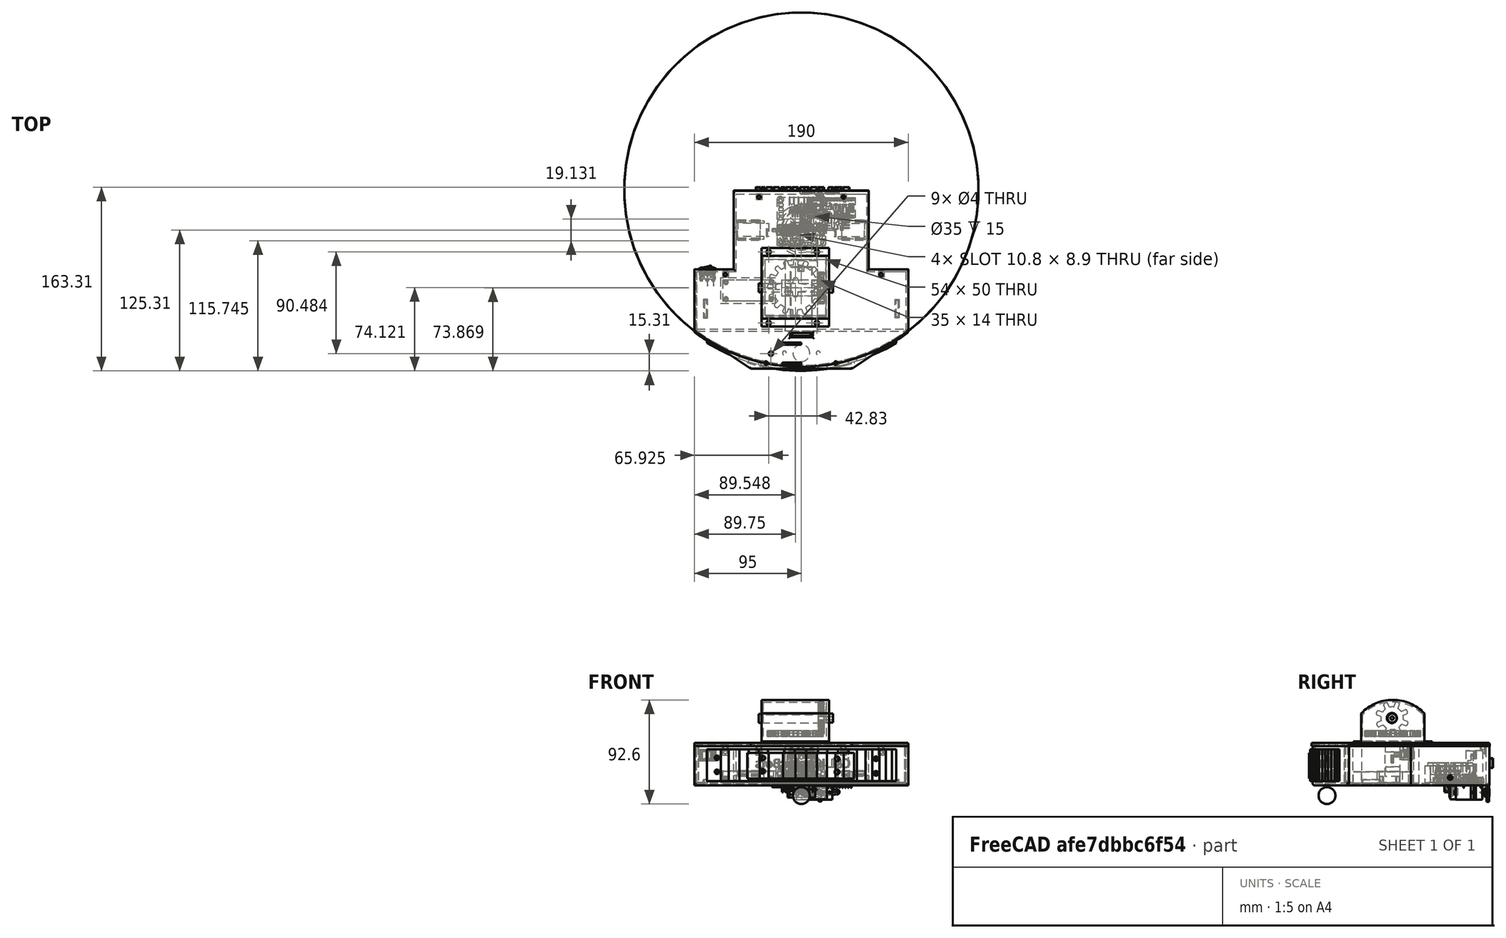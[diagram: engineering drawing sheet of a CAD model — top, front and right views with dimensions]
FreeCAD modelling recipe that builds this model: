
FCSTD DOCUMENT  (FreeCAD 0.20R29410 (Git))
Label: zero_bot
License: All rights reserved
LicenseURL: http://en.wikipedia.org/wiki/All_rights_reserved
objects: Part::Feature×121, Part::Extrusion×56, Sketcher::SketchObject×48, Part::Cut×30, Part::MultiFuse×23, App::Part×10, Part::Box×3, Part::Chamfer×2, Mesh::Feature×2, Part::Part2DObjectPython×1, Part::Fuse×1, Part::Fillet×1, Part::Thickness×1, Part::Sphere×1
note: 288 computed .brp shape members not serialized (recipe doc carries the construction recipe); baked Part::Feature solids carry a one-line shape summary decoded from their .brp

FEATURE [Part::Feature] Part__Feature101  label="Lid Screw Hole001"
  Placement = pos=(159.5,0,0) rot=(0,0,1;0rad)
  shape: bbox 5 x 5 x 8.25 mm, 13 faces (baked)
FEATURE [Part::Feature] Part__Feature102  label="Lid Screw Hole002"
  Placement = pos=(51,69,0) rot=(0,0,1;0rad)
  shape: bbox 5 x 5 x 8.25 mm, 13 faces (baked)
FEATURE [Part::Feature] Part__Feature103  label="Lid Screw Hole003"
  Placement = pos=(126,69,0) rot=(0,0,1;0rad)
  shape: bbox 5 x 5 x 8.25 mm, 13 faces (baked)
FEATURE [Part::Feature] Part__Feature104  label="Lid Screw Hole004"
  Placement = pos=(-120,-158,0) rot=(0,0,1;3.14159rad)
  shape: bbox 5 x 5 x 8.25 mm, 13 faces (baked)
FEATURE [Part::Feature] Part__Feature105  label="Lid Screw Hole005"
  Placement = pos=(-58,-158,0) rot=(0,0,1;3.14159rad)
  shape: bbox 5 x 5 x 8.25 mm, 13 faces (baked)
FEATURE [Part::Feature] Part__Feature106  label="Lid Screw Hole006"
  Placement = pos=(88,5,0) rot=(0,0,1;0rad)
  shape: bbox 5 x 5 x 8.25 mm, 13 faces (baked)
FEATURE [Part::Part2DObjectPython] ShapeString  # Draft 2D object (typed FeaturePython)
  FontFile = <path>
  MakeFace = true
  Placement = pos=(43.52,35,15.82) rot=(0,0.707107,0.707107;3.14159rad)
  Size = 5
  String = C&L KombatBots
  Tracking = 0
FEATURE [Part::Extrusion] Extrude026  label="RobotText"
  Base = -> ShapeString
  Dir = (1e-16,1,4e-16)
  DirMode = 2
  FaceMakerClass = Part::FaceMakerBullseye
  LengthFwd = 3
  LengthRev = 0
  Solid = false
  Symmetric = false
FEATURE [Sketcher::SketchObject] Sketch001
  FullyConstrained = true
  sketch-geometry (10):
    g0: LineSegment StartX=-60 StartY=35 StartZ=0 EndX=60 EndY=35 EndZ=0
    g1: LineSegment StartX=60 StartY=35 StartZ=0 EndX=60 EndY=-35 EndZ=0
    g2: LineSegment StartX=60 StartY=-35 StartZ=0 EndX=95 EndY=-35 EndZ=0
    g3: LineSegment StartX=95 StartY=-35 StartZ=0 EndX=95 EndY=-90 EndZ=0
    g4: LineSegment StartX=95 StartY=-90 StartZ=0 EndX=45 EndY=-123.166 EndZ=0
    g5: LineSegment StartX=45 StartY=-123.166 StartZ=0 EndX=-45 EndY=-123.166 EndZ=0
    g6: LineSegment StartX=-45 StartY=-123.166 StartZ=0 EndX=-95 EndY=-90 EndZ=0
    g7: LineSegment StartX=-95 StartY=-90 StartZ=0 EndX=-95 EndY=-35 EndZ=0
    g8: LineSegment StartX=-95 StartY=-35 StartZ=0 EndX=-60 EndY=-35 EndZ=0
    g9: LineSegment StartX=-60 StartY=-35 StartZ=0 EndX=-60 EndY=35 EndZ=0
  constraints (29):
    c: Horizontal(g0)
    c: Coincident(g0,g1)
    c: Vertical(g1)
    c: Coincident(g1,g2)
    c: Coincident(g2,g3)
    c: Coincident(g3,g4)
    c: Coincident(g4,g5)
    c: Coincident(g5,g6)
    c: Coincident(g6,g7)
    c: Coincident(g7,g8)
    c: Horizontal(g8)
    c: Coincident(g8,g9)
    c: Coincident(g9,g0)
    c: DistanceX(g0,g0) = 120
    c: Vertical(g9)
    c: DistanceY(g9,g9) = 70
    c: DistanceX(g8,g8) = 35
    c: Vertical(g7)
    c: DistanceX(g5,g5) = 90
    c: Horizontal(g5)
    c: Vertical(g3)
    c: DistanceY(g3,g3) = 55
    c: Horizontal(g2)
    c: Equal(g2,g8)
    c: Equal(g9,g1)
    c: Distance(g4) = 60
    c: Equal(g4,g6)
    c: Equal(g3,g7)
    c: Symmetric(g1,g0,g-1)
FEATURE [Part::Extrusion] Extrude001  label="Floor"
  Base = -> Sketch001
  Dir = (0,0,1)
  DirMode = 2
  FaceMakerClass = Part::FaceMakerBullseye
  LengthFwd = 2
  LengthRev = 0
  Solid = true
  Symmetric = false
FEATURE [Sketcher::SketchObject] Sketch002
  FullyConstrained = true
  sketch-geometry (22):
    g0: LineSegment StartX=-60 StartY=35 StartZ=0 EndX=60 EndY=35 EndZ=0
    g1: LineSegment StartX=60 StartY=35 StartZ=0 EndX=60 EndY=-35 EndZ=0
    g2: LineSegment StartX=60 StartY=-35 StartZ=0 EndX=95 EndY=-35 EndZ=0
    g3: LineSegment StartX=95 StartY=-35 StartZ=0 EndX=95 EndY=-90 EndZ=0
    g4: LineSegment StartX=95 StartY=-90 StartZ=0 EndX=45 EndY=-123.166 EndZ=0
    g5: LineSegment StartX=45 StartY=-123.166 StartZ=0 EndX=-45 EndY=-123.166 EndZ=0
    g6: LineSegment StartX=-45 StartY=-123.166 StartZ=0 EndX=-95 EndY=-90 EndZ=0
    g7: LineSegment StartX=-95 StartY=-90 StartZ=0 EndX=-95 EndY=-35 EndZ=0
    g8: LineSegment StartX=-95 StartY=-35 StartZ=0 EndX=-60 EndY=-35 EndZ=0
    g9: LineSegment StartX=-60 StartY=-35 StartZ=0 EndX=-60 EndY=35 EndZ=0
    g10: LineSegment StartX=-58 StartY=32 StartZ=0 EndX=58 EndY=32 EndZ=0
    g11: LineSegment StartX=58 StartY=32 StartZ=0 EndX=58 EndY=-37 EndZ=0
    g12: LineSegment StartX=58 StartY=-37 StartZ=0 EndX=93 EndY=-37 EndZ=0
    g13: LineSegment StartX=93 StartY=-37 StartZ=0 EndX=93 EndY=-89.3266 EndZ=0
    g14: LineSegment StartX=93 StartY=-89.3266 StartZ=0 EndX=45 EndY=-121.166 EndZ=0
    g15: LineSegment StartX=45 StartY=-121.166 StartZ=0 EndX=-45 EndY=-121.166 EndZ=0
    g16: LineSegment StartX=-45 StartY=-121.166 StartZ=0 EndX=-93 EndY=-89.3266 EndZ=0
    g17: LineSegment StartX=-93 StartY=-89.3266 StartZ=0 EndX=-93 EndY=-37 EndZ=0
    g18: LineSegment StartX=-93 StartY=-37 StartZ=0 EndX=-58 EndY=-37 EndZ=0
    g19: LineSegment StartX=-58 StartY=-37 StartZ=0 EndX=-58 EndY=32 EndZ=0
    g20: LineSegment StartX=-45 StartY=-121.166 StartZ=0 EndX=-45 EndY=-123.166 EndZ=0
    g21: LineSegment StartX=45 StartY=-121.166 StartZ=0 EndX=45 EndY=-123.166 EndZ=0
  constraints (63):
    c: Horizontal(g0)
    c: Coincident(g0,g1)
    c: Vertical(g1)
    c: Coincident(g1,g2)
    c: Horizontal(g2)
    c: Coincident(g2,g3)
    c: Vertical(g3)
    c: Coincident(g3,g4)
    c: Coincident(g4,g5)
    c: Horizontal(g5)
    c: Coincident(g5,g6)
    c: Coincident(g6,g7)
    c: Vertical(g7)
    c: Coincident(g7,g8)
    c: Horizontal(g8)
    c: Coincident(g8,g9)
    c: Coincident(g9,g0)
    c: Vertical(g9)
    c: Symmetric(g0,g1,g-1)
    c: DistanceX(g0,g0) = 120
    c: DistanceY(g1,g1) = 70
    c: Equal(g9,g1)
    c: DistanceX(g2,g2) = 35
    c: Equal(g2,g8)
    c: DistanceY(g3,g3) = 55
    c: DistanceX(g5,g5) = 90
    c: Distance(g4) = 60
    c: Equal(g4,g6)
    c: Equal(g3,g7)
    c: Horizontal(g10)
    c: Coincident(g11,g10)
    c: Vertical(g11)
    c: Coincident(g11,g12)
    c: Horizontal(g12)
    c: Coincident(g12,g13)
    c: Vertical(g13)
    c: Coincident(g13,g14)
    c: Coincident(g14,g15)
    c: Horizontal(g15)
    c: Coincident(g15,g16)
    c: Coincident(g16,g17)
    c: Vertical(g17)
    c: Coincident(g17,g18)
    c: Horizontal(g18)
    c: Coincident(g18,g19)
    c: Coincident(g19,g10)
    c: Vertical(g19)
    c: Distance(g10,g0) = 3
    c: Distance(g10,g9) = 2
    c: Distance(g17,g8) = 2
    c: Distance(g16,g7) = 2
    c: Distance(g15,g5) = 2
    c: Distance(g13,g3) = 2
    c: Distance(g12,g2) = 2
    c: Distance(g10,g1) = 2
    c: Coincident(g20,g15)
    c: Coincident(g20,g5)
    c: Coincident(g21,g14)
    c: Coincident(g21,g4)
    c: Vertical(g21)
    c: Vertical(g20)
    c: Parallel(g16,g6)
    c: Parallel(g14,g4)
FEATURE [Part::Extrusion] Extrude002  label="Walls"
  Base = -> Sketch002
  Dir = (0,0,1)
  DirMode = 2
  FaceMakerClass = Part::FaceMakerBullseye
  LengthFwd = 35
  LengthRev = 0
  Solid = true
  Symmetric = false
FEATURE [Part::MultiFuse] Fusion004  label="Body"
  Refine = true
  Shapes = -> [Extrude002,Extrude001]
FEATURE [Sketcher::SketchObject] Sketch003
  FullyConstrained = false
  MapMode = 5
  Placement = pos=(0,0,2) rot=(0,0,1;0rad)
  Support = -> [Fusion004]
  sketch-geometry (36):
    g0: GeomPoint X=25 Y=0 Z=0
    g1: LineSegment StartX=33 StartY=6 StartZ=0 EndX=58 EndY=6 EndZ=0
    g2: LineSegment StartX=58 StartY=6 StartZ=0 EndX=58 EndY=8 EndZ=0
    g3: LineSegment StartX=58 StartY=8 StartZ=0 EndX=33 EndY=8 EndZ=0
    g4: LineSegment StartX=33 StartY=8 StartZ=0 EndX=33 EndY=6 EndZ=0
    g5: GeomPoint X=-25 Y=0 Z=0
    g6: LineSegment StartX=33 StartY=6 StartZ=0 EndX=25 EndY=0 EndZ=0
    g7: GeomPoint X=25 Y=0 Z=0
    g8: LineSegment StartX=32.5993 StartY=-6.5 StartZ=0 EndX=25 EndY=0 EndZ=0
    g9: GeomPoint X=-25 Y=0 Z=0
    g10: GeomPoint X=-25 Y=0 Z=0
    g11: GeomPoint X=25 Y=0 Z=0
    g12: LineSegment StartX=33 StartY=-6 StartZ=0 EndX=58 EndY=-6 EndZ=0
    g13: LineSegment StartX=58 StartY=-6 StartZ=0 EndX=58 EndY=-8 EndZ=0
    g14: LineSegment StartX=58 StartY=-8 StartZ=0 EndX=33 EndY=-8 EndZ=0
    g15: LineSegment StartX=33 StartY=-8 StartZ=0 EndX=33 EndY=-6 EndZ=0
    g16: LineSegment StartX=33 StartY=-6 StartZ=0 EndX=25 EndY=0 EndZ=0
    g17: GeomPoint X=25 Y=0 Z=0
    g18: LineSegment StartX=32.5993 StartY=6.5 StartZ=0 EndX=25 EndY=0 EndZ=0
    g19: GeomPoint X=-25 Y=0 Z=0
    g20: LineSegment StartX=-33 StartY=6 StartZ=0 EndX=-58 EndY=6 EndZ=0
    g21: LineSegment StartX=-58 StartY=6 StartZ=0 EndX=-58 EndY=8 EndZ=0
    g22: LineSegment StartX=-58 StartY=8 StartZ=0 EndX=-33 EndY=8 EndZ=0
    g23: LineSegment StartX=-33 StartY=8 StartZ=0 EndX=-33 EndY=6 EndZ=0
    g24: LineSegment StartX=-33 StartY=6 StartZ=0 EndX=-25 EndY=0 EndZ=0
    g25: GeomPoint X=-25 Y=0 Z=0
    g26: LineSegment StartX=-32.5993 StartY=-6.5 StartZ=0 EndX=-25 EndY=0 EndZ=0
    g27: GeomPoint X=-25 Y=0 Z=0
    g28: LineSegment StartX=-33 StartY=-6 StartZ=0 EndX=-58 EndY=-6 EndZ=0
    g29: LineSegment StartX=-58 StartY=-6 StartZ=0 EndX=-58 EndY=-8 EndZ=0
    g30: LineSegment StartX=-58 StartY=-8 StartZ=0 EndX=-33 EndY=-8 EndZ=0
    g31: LineSegment StartX=-33 StartY=-8 StartZ=0 EndX=-33 EndY=-6 EndZ=0
    g32: LineSegment StartX=-33 StartY=-6 StartZ=0 EndX=-25 EndY=0 EndZ=0
    g33: GeomPoint X=-25 Y=0 Z=0
    g34: LineSegment StartX=-32.5993 StartY=6.5 StartZ=0 EndX=-25 EndY=0 EndZ=0
    g35: LineSegment StartX=-33 StartY=8 StartZ=0 EndX=-33 EndY=-8 EndZ=0
  constraints (60):
    c: PointOnObject(g0,g-1)
    c: Distance(g-1,g0) = 25
    c: Coincident(g1,g2)
    c: Coincident(g2,g3)
    c: Coincident(g3,g4)
    c: Coincident(g4,g1)
    c: Horizontal(g1)
    c: Horizontal(g3)
    c: Vertical(g2)
    c: Vertical(g4)
    c: DistanceY(g4,g4) = 2
    c: DistanceX(g1,g1) = 25
    c: Coincident(g6,g1)
    c: Coincident(g6,g0)
    c: Distance(g6) = 10
    c: DistanceY(g-1,g1) = 6
    c: Coincident(g8,g7)
    c: Distance(g8) = 10
    c: Coincident(g12,g13)
    c: Coincident(g13,g14)
    c: Coincident(g14,g15)
    c: Coincident(g15,g12)
    c: Horizontal(g12)
    c: Horizontal(g14)
    c: Vertical(g13)
    c: Vertical(g15)
    c: Coincident(g16,g12)
    c: Coincident(g16,g11)
    c: Distance(g16) = 10
    c: Coincident(g18,g17)
    c: Distance(g18) = 10
    c: Coincident(g20,g21)
    c: Coincident(g21,g22)
    c: Coincident(g22,g23)
    c: Coincident(g23,g20)
    c: Horizontal(g20)
    c: Horizontal(g22)
    c: Vertical(g21)
    c: Vertical(g23)
    c: Coincident(g24,g20)
    c: Coincident(g24,g19)
    c: Distance(g24) = 10
    c: Coincident(g26,g25)
    c: Distance(g26) = 10
    c: Coincident(g28,g29)
    c: Coincident(g29,g30)
    c: Coincident(g30,g31)
    c: Coincident(g31,g28)
    c: Horizontal(g28)
    c: Horizontal(g30)
    c: Vertical(g29)
    c: Vertical(g31)
    c: Coincident(g32,g28)
    c: Coincident(g32,g27)
    c: Distance(g32) = 10
    c: Coincident(g34,g33)
    c: Distance(g34) = 10
    c: Coincident(g35,g22)
    c: Coincident(g35,g30)
    c: Vertical(g35)
FEATURE [Part::Extrusion] Extrude003  label="motorWalls"
  Base = -> Sketch003
  Dir = (0,0,1)
  DirMode = 2
  FaceMakerClass = Part::FaceMakerBullseye
  LengthFwd = 10
  LengthRev = 0
  Solid = true
  Symmetric = false
FEATURE [Sketcher::SketchObject] Sketch004
  FullyConstrained = false
  MapMode = 5
  Placement = pos=(0,0,2) rot=(0,0,1;0rad)
  Support = -> [Fusion004]
  sketch-geometry (10):
    g0: LineSegment StartX=-31 StartY=6 StartZ=0 EndX=-29 EndY=6 EndZ=0
    g1: LineSegment StartX=-29 StartY=6 StartZ=0 EndX=-29 EndY=-6 EndZ=0
    g2: LineSegment StartX=-29 StartY=-6 StartZ=0 EndX=-31 EndY=-6 EndZ=0
    g3: LineSegment StartX=-31 StartY=-6 StartZ=0 EndX=-31 EndY=6 EndZ=0
    g4: GeomPoint X=-30 Y=0 Z=0
    g5: LineSegment StartX=31 StartY=6 StartZ=0 EndX=29 EndY=6 EndZ=0
    g6: LineSegment StartX=29 StartY=6 StartZ=0 EndX=29 EndY=-6 EndZ=0
    g7: LineSegment StartX=29 StartY=-6 StartZ=0 EndX=31 EndY=-6 EndZ=0
    g8: LineSegment StartX=31 StartY=-6 StartZ=0 EndX=31 EndY=6 EndZ=0
    g9: GeomPoint X=30 Y=0 Z=0
  constraints (22):
    c: Coincident(g0,g1)
    c: Coincident(g1,g2)
    c: Coincident(g2,g3)
    c: Coincident(g3,g0)
    c: Horizontal(g0)
    c: Horizontal(g2)
    c: Vertical(g1)
    c: Vertical(g3)
    c: PointOnObject(g4,g-1)
    c: Distance(g-1,g4) = 30
    c: Symmetric(g0,g2,g4)
    c: DistanceX(g0,g0) = 2
    c: DistanceY(g1,g1) = 12
    c: Coincident(g5,g6)
    c: Coincident(g6,g7)
    c: Coincident(g7,g8)
    c: Coincident(g8,g5)
    c: Horizontal(g5)
    c: Horizontal(g7)
    c: Vertical(g6)
    c: Vertical(g8)
    c: Symmetric(g5,g7,g9)
FEATURE [Part::Extrusion] Extrude004
  Base = -> Sketch004
  Dir = (0,0,1)
  DirMode = 2
  FaceMakerClass = Part::FaceMakerBullseye
  LengthFwd = 3
  LengthRev = 0
  Solid = true
  Symmetric = false
FEATURE [Part::Chamfer] Chamfer  label="MotorSlotter"
  Base = -> Extrude004
  Edges = 2 edges r=1: [Edge12,Edge24]
FEATURE [Part::MultiFuse] Fusion001  label="MotorHolders"
  Refine = true
  Shapes = -> [Chamfer,Extrude003]
FEATURE [Part::MultiFuse] Fusion005
  Refine = true
  Shapes = -> [Fusion001,Fusion004]
FEATURE [Sketcher::SketchObject] Sketch005
  FullyConstrained = true
  MapMode = 5
  Placement = pos=(0,0,2) rot=(0,0,1;0rad)
  Support = -> [Fusion005]
  sketch-geometry (8):
    g0: Circle CenterX=-18.8 CenterY=26.75 CenterZ=0 NormalX=0 NormalY=0 NormalZ=1 AngleXU=0 Radius=3
    g1: Circle CenterX=-18.8 CenterY=26.75 CenterZ=0 NormalX=0 NormalY=0 NormalZ=1 AngleXU=0 Radius=1.5
    g2: Circle CenterX=18.8 CenterY=26.75 CenterZ=0 NormalX=0 NormalY=0 NormalZ=1 AngleXU=0 Radius=3
    g3: Circle CenterX=18.8 CenterY=26.75 CenterZ=0 NormalX=0 NormalY=0 NormalZ=1 AngleXU=0 Radius=1.5
    g4: Circle CenterX=18.8 CenterY=-11 CenterZ=0 NormalX=0 NormalY=0 NormalZ=1 AngleXU=0 Radius=3
    g5: Circle CenterX=18.8 CenterY=-11 CenterZ=0 NormalX=0 NormalY=0 NormalZ=1 AngleXU=0 Radius=1.5
    g6: Circle CenterX=-18.8 CenterY=-11 CenterZ=0 NormalX=0 NormalY=0 NormalZ=1 AngleXU=0 Radius=3
    g7: Circle CenterX=-18.8 CenterY=-11 CenterZ=0 NormalX=0 NormalY=0 NormalZ=1 AngleXU=0 Radius=1.5
  constraints (20):
    c: Coincident(g1,g0)
    c: Coincident(g3,g2)
    c: Coincident(g5,g4)
    c: Coincident(g7,g6)
    c: DistanceX(g-2,g6) = -18.8
    c: Diameter(g7) = 3
    c: Diameter(g6) = 6
    c: DistanceY(g-1,g6) = -11
    c: DistanceY(g-1,g4) = -11
    c: DistanceX(g-2,g4) = 18.8
    c: Diameter(g5) = 3
    c: Diameter(g4) = 6
    c: DistanceY(g-1,g2) = 26.75
    c: DistanceY(g-1,g0) = 26.75
    c: DistanceX(g-2,g2) = 18.8
    c: DistanceX(g-2,g0) = -18.8
    c: Diameter(g1) = 3
    c: Diameter(g0) = 6
    c: Diameter(g2) = 6
    c: Diameter(g3) = 3
FEATURE [Part::Extrusion] Extrude005  label="L289N Holder"
  Base = -> Sketch005
  Dir = (0,0,1)
  DirMode = 2
  FaceMakerClass = Part::FaceMakerBullseye
  LengthFwd = 4
  LengthRev = 0
  Solid = true
  Symmetric = false
FEATURE [Part::MultiFuse] Fusion006
  Refine = true
  Shapes = -> [Extrude005,Fusion005]
FEATURE [Sketcher::SketchObject] Sketch006
  FullyConstrained = true
  MapMode = 5
  Placement = pos=(60,0,0) rot=(0.57735,0.57735,0.57735;2.0944rad)
  Support = -> [Fusion006]
  sketch-geometry (1):
    g0: Circle CenterX=0 CenterY=7 CenterZ=0 NormalX=0 NormalY=0 NormalZ=1 AngleXU=0 Radius=2
  constraints (3):
    c: PointOnObject(g0,g-2)
    c: Diameter(g0) = 4
    c: Distance(g0,g-1) = 7
FEATURE [Part::Extrusion] Extrude006
  Base = -> Sketch006
  Dir = (1,0,0)
  DirMode = 2
  FaceMakerClass = Part::FaceMakerBullseye
  LengthFwd = 10
  LengthRev = 0
  Solid = true
  Symmetric = true
FEATURE [Sketcher::SketchObject] Sketch007
  FullyConstrained = true
  MapMode = 5
  Placement = pos=(-60,0,0) rot=(0.57735,-0.57735,-0.57735;2.0944rad)
  Support = -> [Fusion006]
  sketch-geometry (1):
    g0: Circle CenterX=0 CenterY=7 CenterZ=0 NormalX=0 NormalY=0 NormalZ=1 AngleXU=0 Radius=2
  constraints (3):
    c: PointOnObject(g0,g-2)
    c: Diameter(g0) = 4
    c: Distance(g-1,g0) = 7
FEATURE [Part::Extrusion] Extrude007
  Base = -> Sketch007
  Dir = (-1,0,0)
  DirMode = 2
  FaceMakerClass = Part::FaceMakerBullseye
  LengthFwd = 10
  LengthRev = 0
  Solid = true
  Symmetric = true
FEATURE [Part::MultiFuse] Fusion007  label="Motor Gaps"
  Refine = true
  Shapes = -> [Extrude006,Extrude007]
FEATURE [Part::Cut] Cut005
  Base = -> Fusion006
  Refine = true
  Tool = -> Fusion007
FEATURE [Sketcher::SketchObject] Sketch008
  FullyConstrained = false
  MapMode = 5
  Placement = pos=(0,-35,0) rot=(0,0.707107,0.707107;3.14159rad)
  Support = -> [Cut005]
  sketch-geometry (4):
    g0: LineSegment StartX=90.8327 StartY=31.6367 StartZ=0 EndX=76.0827 EndY=31.6367 EndZ=0
    g1: LineSegment StartX=76.0827 StartY=31.6367 StartZ=0 EndX=76.0827 EndY=21.8867 EndZ=0
    g2: LineSegment StartX=76.0827 StartY=21.8867 StartZ=0 EndX=90.8327 EndY=21.8867 EndZ=0
    g3: LineSegment StartX=90.8327 StartY=21.8867 StartZ=0 EndX=90.8327 EndY=31.6367 EndZ=0
  constraints (8):
    c: Coincident(g0,g1)
    c: Coincident(g1,g2)
    c: Coincident(g2,g3)
    c: Coincident(g3,g0)
    c: Horizontal(g0)
    c: Horizontal(g2)
    c: Vertical(g1)
    c: Vertical(g3)
FEATURE [Part::Extrusion] Extrude008  label="InterruptGap"
  Base = -> Sketch008
  Dir = (0,1,-2e-16)
  DirMode = 2
  FaceMakerClass = Part::FaceMakerBullseye
  LengthFwd = 10
  LengthRev = 0
  Solid = true
  Symmetric = true
FEATURE [Part::Cut] Cut006
  Base = -> Cut005
  Refine = true
  Tool = -> Extrude008
FEATURE [Sketcher::SketchObject] Sketch009
  FullyConstrained = false
  MapMode = 5
  Placement = pos=(0,0,2) rot=(0,0,1;0rad)
  Support = -> [Cut006]
  sketch-geometry (20):
    g0: LineSegment StartX=83.4 StartY=-61.75 StartZ=0 EndX=87 EndY=-61.75 EndZ=0
    g1: LineSegment StartX=87 StartY=-61.75 StartZ=0 EndX=87 EndY=-78.25 EndZ=0
    g2: LineSegment StartX=87 StartY=-78.25 StartZ=0 EndX=83.4 EndY=-78.25 EndZ=0
    g3: LineSegment StartX=83.4 StartY=-78.25 StartZ=0 EndX=83.4 EndY=-61.75 EndZ=0
    g4: LineSegment StartX=84.4 StartY=-62.6 StartZ=0 EndX=86 EndY=-62.6 EndZ=0
    g5: LineSegment StartX=86 StartY=-62.6 StartZ=0 EndX=86 EndY=-77.4 EndZ=0
    g6: LineSegment StartX=86 StartY=-77.4 StartZ=0 EndX=84.4 EndY=-77.4 EndZ=0
    g7: LineSegment StartX=84.4 StartY=-77.4 StartZ=0 EndX=84.4 EndY=-62.6 EndZ=0
    g8: GeomPoint X=93 Y=-70 Z=0
    g9: LineSegment StartX=-0.686599 StartY=-70 StartZ=0 EndX=93 EndY=-70 EndZ=0
    g10: LineSegment StartX=-83.4 StartY=-61.75 StartZ=0 EndX=-87 EndY=-61.75 EndZ=0
    g11: LineSegment StartX=-87 StartY=-61.75 StartZ=0 EndX=-87 EndY=-78.25 EndZ=0
    g12: LineSegment StartX=-87 StartY=-78.25 StartZ=0 EndX=-83.4 EndY=-78.25 EndZ=0
    g13: LineSegment StartX=-83.4 StartY=-78.25 StartZ=0 EndX=-83.4 EndY=-61.75 EndZ=0
    g14: LineSegment StartX=-84.4 StartY=-62.6 StartZ=0 EndX=-86 EndY=-62.6 EndZ=0
    g15: LineSegment StartX=-86 StartY=-62.6 StartZ=0 EndX=-86 EndY=-77.4 EndZ=0
    g16: LineSegment StartX=-86 StartY=-77.4 StartZ=0 EndX=-84.4 EndY=-77.4 EndZ=0
    g17: LineSegment StartX=-84.4 StartY=-77.4 StartZ=0 EndX=-84.4 EndY=-62.6 EndZ=0
    g18: GeomPoint X=-93 Y=-70 Z=0
    g19: LineSegment StartX=0.686599 StartY=-70 StartZ=0 EndX=-93 EndY=-70 EndZ=0
  constraints (46):
    c: Coincident(g0,g1)
    c: Coincident(g1,g2)
    c: Coincident(g2,g3)
    c: Coincident(g3,g0)
    c: Horizontal(g0)
    c: Horizontal(g2)
    c: Vertical(g1)
    c: Vertical(g3)
    c: Coincident(g4,g5)
    c: Coincident(g5,g6)
    c: Coincident(g6,g7)
    c: Coincident(g7,g4)
    c: Horizontal(g4)
    c: Horizontal(g6)
    c: Vertical(g7)
    c: DistanceX(g-2,g8) = 93
    c: DistanceY(g-1,g8) = -70
    c: Distance(g8,g1) = 6
    c: Coincident(g9,g8)
    c: Symmetric(g1,g0,g9)
    c: DistanceY(g1,g1) = 16.5
    c: Symmetric(g4,g5,g9)
    c: DistanceY(g5,g5) = 14.8
    c: DistanceX(g0,g0) = 3.6
    c: DistanceX(g4,g4) = 1.6
    c: Distance(g4,g1) = 1
    c: Coincident(g10,g11)
    c: Coincident(g11,g12)
    c: Coincident(g12,g13)
    c: Coincident(g13,g10)
    c: Horizontal(g10)
    c: Horizontal(g12)
    c: Vertical(g11)
    c: Vertical(g13)
    c: Coincident(g14,g15)
    c: Coincident(g15,g16)
    c: Coincident(g16,g17)
    c: Coincident(g17,g14)
    c: Horizontal(g14)
    c: Horizontal(g16)
    c: Vertical(g17)
    c: Distance(g18,g11) = 6
    c: Coincident(g19,g18)
    c: Symmetric(g11,g10,g19)
    c: Symmetric(g14,g15,g19)
    c: Distance(g14,g11) = 1
FEATURE [Part::Extrusion] Extrude009  label="HitSensorHolders"
  Base = -> Sketch009
  Dir = (0,0,1)
  DirMode = 2
  FaceMakerClass = Part::FaceMakerBullseye
  LengthFwd = 3
  LengthRev = 0
  Solid = true
  Symmetric = false
FEATURE [Part::MultiFuse] Fusion008
  Refine = true
  Shapes = -> [Cut006,Extrude009]
FEATURE [Sketcher::SketchObject] Sketch010
  FullyConstrained = true
  sketch-geometry (11):
    g0: LineSegment StartX=-14.5 StartY=-78.5 StartZ=0 EndX=-9.5 EndY=-78.5 EndZ=0
    g1: LineSegment StartX=-9.5 StartY=-78.5 StartZ=0 EndX=-9.5 EndY=-32.5 EndZ=0
    g2: LineSegment StartX=-9.5 StartY=-32.5 StartZ=0 EndX=9.5 EndY=-32.5 EndZ=0
    g3: LineSegment StartX=9.5 StartY=-32.5 StartZ=0 EndX=9.5 EndY=-86.5 EndZ=0
    g4: LineSegment StartX=9.5 StartY=-86.5 StartZ=0 EndX=-14.5 EndY=-86.5 EndZ=0
    g5: LineSegment StartX=-14.5 StartY=-86.5 StartZ=0 EndX=-14.5 EndY=-91.5 EndZ=0
    g6: LineSegment StartX=-14.5 StartY=-91.5 StartZ=0 EndX=14.5 EndY=-91.5 EndZ=0
    g7: LineSegment StartX=14.5 StartY=-91.5 StartZ=0 EndX=14.5 EndY=-27.5 EndZ=0
    g8: LineSegment StartX=14.5 StartY=-27.5 StartZ=0 EndX=-14.5 EndY=-27.5 EndZ=0
    g9: LineSegment StartX=-14.5 StartY=-27.5 StartZ=0 EndX=-14.5 EndY=-78.5 EndZ=0
    g10: GeomPoint X=0 Y=-59.5 Z=0
  constraints (30):
    c: Horizontal(g0)
    c: Coincident(g0,g1)
    c: Vertical(g1)
    c: Coincident(g1,g2)
    c: Horizontal(g2)
    c: Coincident(g2,g3)
    c: Vertical(g3)
    c: Coincident(g3,g4)
    c: Horizontal(g4)
    c: Coincident(g4,g5)
    c: Vertical(g5)
    c: Coincident(g5,g6)
    c: Horizontal(g6)
    c: Coincident(g6,g7)
    c: Vertical(g7)
    c: Coincident(g7,g8)
    c: Horizontal(g8)
    c: Coincident(g8,g9)
    c: Coincident(g9,g0)
    c: Vertical(g9)
    c: DistanceX(g2,g2) = 19
    c: PointOnObject(g10,g-2)
    c: DistanceY(g10,g-1) = 59.5
    c: Symmetric(g3,g1,g10)
    c: Symmetric(g6,g8,g10)
    c: DistanceX(g8,g8) = 29
    c: DistanceY(g3,g3) = 54
    c: DistanceY(g7,g7) = 64
    c: DistanceY(g1,g1) = 46
    c: DistanceX(g6,g6) = 29
FEATURE [Part::Extrusion] Extrude010  label="Battery Gap"
  Base = -> Sketch010
  Dir = (0,0,1)
  DirMode = 2
  FaceMakerClass = Part::FaceMakerBullseye
  LengthFwd = 35
  LengthRev = 0
  Solid = true
  Symmetric = false
FEATURE [Part::MultiFuse] Fusion009
  Refine = true
  Shapes = -> [Extrude010,Fusion008]
FEATURE [Sketcher::SketchObject] Sketch011
  FullyConstrained = false
  MapMode = 5
  Placement = pos=(0,0,2) rot=(0,0,1;0rad)
  Support = -> [Fusion009]
  sketch-geometry (13):
    g0: LineSegment StartX=-52.8 StartY=-54 StartZ=0 EndX=0 EndY=-54 EndZ=0
    g1: LineSegment StartX=-52.8 StartY=-54 StartZ=0 EndX=-84.748 EndY=-54 EndZ=0
    g2: Circle CenterX=-66.9946 CenterY=-46.5 CenterZ=0 NormalX=0 NormalY=0 NormalZ=1 AngleXU=0 Radius=1
    g3: Circle CenterX=-66.9946 CenterY=-46.5 CenterZ=0 NormalX=0 NormalY=0 NormalZ=1 AngleXU=0 Radius=2
    g4: Circle CenterX=-66.9946 CenterY=-61.5 CenterZ=0 NormalX=0 NormalY=0 NormalZ=1 AngleXU=0 Radius=1
    g5: Circle CenterX=-66.9946 CenterY=-61.5 CenterZ=0 NormalX=0 NormalY=0 NormalZ=1 AngleXU=0 Radius=2
    g6: GeomPoint X=-25.3 Y=-54 Z=0
    g7: Circle CenterX=-26.6711 CenterY=-46.5 CenterZ=0 NormalX=0 NormalY=0 NormalZ=1 AngleXU=0 Radius=1
    g8: Circle CenterX=-26.6711 CenterY=-46.5 CenterZ=0 NormalX=0 NormalY=0 NormalZ=1 AngleXU=0 Radius=2
    g9: Circle CenterX=-26.6711 CenterY=-61.5 CenterZ=0 NormalX=0 NormalY=0 NormalZ=1 AngleXU=0 Radius=1
    g10: Circle CenterX=-26.6711 CenterY=-61.5 CenterZ=0 NormalX=0 NormalY=0 NormalZ=1 AngleXU=0 Radius=2
    g11: LineSegment StartX=-52.8 StartY=-54 StartZ=0 EndX=0 EndY=-54 EndZ=0
    g12: GeomPoint X=-25.3 Y=-54 Z=0
  constraints (24):
    c: DistanceY(g0,g-1) = 54
    c: PointOnObject(g0,g-2)
    c: Horizontal(g0)
    c: Coincident(g1,g0)
    c: Horizontal(g1)
    c: Coincident(g3,g2)
    c: Diameter(g2) = 2
    c: Diameter(g3) = 4
    c: Distance(g2,g1) = 7.5
    c: Coincident(g5,g4)
    c: Diameter(g4) = 2
    c: Diameter(g5) = 4
    c: PointOnObject(g6,g0)
    c: DistanceX(g6,g-1) = 25.3
    c: Coincident(g8,g7)
    c: Diameter(g7) = 2
    c: Diameter(g8) = 4
    c: Distance(g7,g0) = 7.5
    c: Horizontal(g11)
    c: PointOnObject(g12,g11)
    c: Coincident(g10,g9)
    c: Diameter(g9) = 2
    c: Diameter(g10) = 4
    c: Distance(g9,g11) = 7.5
FEATURE [Part::Extrusion] Extrude011  label="Arduino Holder"
  Base = -> Sketch011
  Dir = (0,0,1)
  DirMode = 2
  FaceMakerClass = Part::FaceMakerBullseye
  LengthFwd = 6
  LengthRev = 0
  Solid = true
  Symmetric = false
FEATURE [Part::MultiFuse] Fusion010
  Refine = true
  Shapes = -> [Fusion009,Extrude011]
FEATURE [Sketcher::SketchObject] Sketch012
  FullyConstrained = true
  MapMode = 5
  Placement = pos=(0,-91.5,0) rot=(1,0,0;1.5708rad)
  Support = -> [Extrude010]
  sketch-geometry (10):
    g0: LineSegment StartX=8 StartY=35 StartZ=0 EndX=10 EndY=35 EndZ=0
    g1: LineSegment StartX=10 StartY=35 StartZ=0 EndX=10 EndY=2 EndZ=0
    g2: LineSegment StartX=10 StartY=2 StartZ=0 EndX=-10 EndY=2 EndZ=0
    g3: LineSegment StartX=-10 StartY=2 StartZ=0 EndX=-10 EndY=35 EndZ=0
    g4: LineSegment StartX=-10 StartY=35 StartZ=0 EndX=-8 EndY=35 EndZ=0
    g5: LineSegment StartX=-8 StartY=35 StartZ=0 EndX=-8 EndY=4 EndZ=0
    g6: LineSegment StartX=-8 StartY=4 StartZ=0 EndX=8 EndY=4 EndZ=0
    g7: LineSegment StartX=8 StartY=4 StartZ=0 EndX=8 EndY=35 EndZ=0
    g8: GeomPoint X=0 Y=2 Z=0
    g9: LineSegment StartX=0 StartY=2 StartZ=0 EndX=0 EndY=0 EndZ=0
  constraints (28):
    c: Horizontal(g0)
    c: Coincident(g0,g1)
    c: Vertical(g1)
    c: Coincident(g1,g2)
    c: Coincident(g2,g3)
    c: Vertical(g3)
    c: Coincident(g3,g4)
    c: Horizontal(g4)
    c: Coincident(g4,g5)
    c: Vertical(g5)
    c: Coincident(g5,g6)
    c: Horizontal(g6)
    c: Coincident(g6,g7)
    c: Coincident(g7,g0)
    c: Vertical(g7)
    c: DistanceX(g0,g0) = 2
    c: Equal(g4,g0)
    c: DistanceX(g6,g6) = 16
    c: DistanceY(g1,g1) = 33
    c: Equal(g3,g1)
    c: Distance(g6,g2) = 2
    c: Horizontal(g2)
    c: PointOnObject(g8,g2)
    c: DistanceX(g8,g1) = 10
    c: DistanceY(g-1,g1) = 2
    c: Coincident(g9,g8)
    c: Coincident(g9,g-1)
    c: Vertical(g9)
FEATURE [Part::Extrusion] Extrude012  label="Bluetooth Module Holder"
  Base = -> Sketch012
  Dir = (0,-1,2e-16)
  DirMode = 2
  FaceMakerClass = Part::FaceMakerBullseye
  LengthFwd = 4
  LengthRev = 0
  Solid = true
  Symmetric = false
FEATURE [Part::MultiFuse] Fusion011
  Refine = true
  Shapes = -> [Fusion010,Extrude012]
FEATURE [Sketcher::SketchObject] Sketch013
  FullyConstrained = false
  MapMode = 5
  Placement = pos=(4.907e-13,3.136e-13,35) rot=(0,0,1;0rad)
  Support = -> [Fusion011]
  sketch-geometry (8):
    g0: LineSegment StartX=8 StartY=-92.5 StartZ=0 EndX=8.5 EndY=-92.5 EndZ=0
    g1: LineSegment StartX=8.5 StartY=-92.5 StartZ=0 EndX=8.5 EndY=-94.7 EndZ=0
    g2: LineSegment StartX=8.5 StartY=-94.7 StartZ=0 EndX=8 EndY=-94.7 EndZ=0
    g3: LineSegment StartX=8 StartY=-94.7 StartZ=0 EndX=8 EndY=-92.5 EndZ=0
    g4: LineSegment StartX=-8 StartY=-92.5 StartZ=0 EndX=-8.5 EndY=-92.5 EndZ=0
    g5: LineSegment StartX=-8.5 StartY=-92.5 StartZ=0 EndX=-8.5 EndY=-94.7 EndZ=0
    g6: LineSegment StartX=-8.5 StartY=-94.7 StartZ=0 EndX=-8 EndY=-94.7 EndZ=0
    g7: LineSegment StartX=-8 StartY=-94.7 StartZ=0 EndX=-8 EndY=-92.5 EndZ=0
  constraints (20):
    c: Coincident(g0,g1)
    c: Coincident(g1,g2)
    c: Coincident(g2,g3)
    c: Coincident(g3,g0)
    c: Horizontal(g0)
    c: Horizontal(g2)
    c: Vertical(g1)
    c: Vertical(g3)
    c: DistanceY(g1,g1) = 2.2
    c: DistanceX(g0,g0) = 0.5
    c: DistanceX(g-2,g0) = 8
    c: DistanceY(g-1,g0) = -92.5
    c: Coincident(g4,g5)
    c: Coincident(g5,g6)
    c: Coincident(g6,g7)
    c: Coincident(g7,g4)
    c: Horizontal(g4)
    c: Horizontal(g6)
    c: Vertical(g5)
    c: Vertical(g7)
FEATURE [Part::Extrusion] Extrude013  label="Bluetooth Module Slotter"
  Base = -> Sketch013
  Dir = (1.4e-14,9e-15,1)
  DirMode = 2
  FaceMakerClass = Part::FaceMakerBullseye
  LengthFwd = -32
  LengthRev = 0
  Solid = true
  Symmetric = false
FEATURE [Part::Cut] Cut007
  Base = -> Fusion011
  Refine = true
  Tool = -> Extrude013
FEATURE [Sketcher::SketchObject] Sketch014
  FullyConstrained = false
  MapMode = 5
  Placement = pos=(0,-37,0) rot=(1,0,0;1.5708rad)
  Support = -> [Cut007]
  sketch-geometry (4):
    g0: LineSegment StartX=-91.0267 StartY=31.7549 StartZ=0 EndX=-86.0267 EndY=31.7549 EndZ=0
    g1: LineSegment StartX=-86.0267 StartY=31.7549 StartZ=0 EndX=-86.0267 EndY=26.7549 EndZ=0
    g2: LineSegment StartX=-86.0267 StartY=26.7549 StartZ=0 EndX=-91.0267 EndY=26.7549 EndZ=0
    g3: LineSegment StartX=-91.0267 StartY=26.7549 StartZ=0 EndX=-91.0267 EndY=31.7549 EndZ=0
  constraints (10):
    c: Coincident(g0,g1)
    c: Coincident(g1,g2)
    c: Coincident(g2,g3)
    c: Coincident(g3,g0)
    c: Horizontal(g0)
    c: Horizontal(g2)
    c: Vertical(g1)
    c: Vertical(g3)
    c: DistanceX(g0,g0) = 5
    c: DistanceY(g1,g1) = 5
FEATURE [Part::Extrusion] Extrude014
  Base = -> Sketch014
  Dir = (0,-1,2e-16)
  DirMode = 2
  FaceMakerClass = Part::FaceMakerBullseye
  LengthFwd = 5
  LengthRev = 0
  Solid = true
  Symmetric = false
FEATURE [Part::Chamfer] Chamfer001  label="Bot Screw Holder"
  Base = -> Extrude014
  Edges = 1 edges r=4.99: [Edge10]
FEATURE [Sketcher::SketchObject] Sketch015
  FullyConstrained = true
  MapMode = 5
  Placement = pos=(0,7e-15,31.7549) rot=(0,0,1;0rad)
  Support = -> [Chamfer001]
  sketch-geometry (1):
    g0: Circle CenterX=-88.6 CenterY=-39.7 CenterZ=0 NormalX=0 NormalY=0 NormalZ=1 AngleXU=0 Radius=1.5
  constraints (3):
    c: Diameter(g0) = 3
    c: DistanceX(g-2,g0) = -88.6
    c: DistanceY(g-1,g0) = -39.7
FEATURE [Part::Extrusion] Extrude015  label="Screw Hole"
  Base = -> Sketch015
  Dir = (0,2e-16,1)
  DirMode = 2
  FaceMakerClass = Part::FaceMakerBullseye
  LengthFwd = -8
  LengthRev = 0
  Placement = pos=(0,0,4.5) rot=(0,0,1;0rad)
  Solid = true
  Symmetric = false
FEATURE [Sketcher::SketchObject] Sketch016
  FullyConstrained = false
  MapMode = 5
  Placement = pos=(0,7e-15,31.7549) rot=(0,0,1;0rad)
  Support = -> [Chamfer001]
  sketch-geometry (4):
    g0: LineSegment StartX=-91.0267 StartY=-37 StartZ=0 EndX=-86.0267 EndY=-37 EndZ=0
    g1: LineSegment StartX=-86.0267 StartY=-37 StartZ=0 EndX=-86.0267 EndY=-42 EndZ=0
    g2: LineSegment StartX=-86.0267 StartY=-42 StartZ=0 EndX=-91.0267 EndY=-42 EndZ=0
    g3: LineSegment StartX=-91.0267 StartY=-42 StartZ=0 EndX=-91.0267 EndY=-37 EndZ=0
  constraints (10):
    c: Coincident(g0,g1)
    c: Coincident(g1,g2)
    c: Coincident(g2,g3)
    c: Coincident(g3,g0)
    c: Horizontal(g0)
    c: Horizontal(g2)
    c: Vertical(g1)
    c: Vertical(g3)
    c: DistanceY(g1,g1) = 5
    c: DistanceX(g2,g2) = 5
FEATURE [Part::Extrusion] Extrude016  label="Top Screw Holder"
  Base = -> Sketch016
  Dir = (0,2e-16,1)
  DirMode = 2
  FaceMakerClass = Part::FaceMakerBullseye
  LengthFwd = 3.25
  LengthRev = 0
  Solid = true
  Symmetric = false
FEATURE [Part::Fuse] Fusion012
  Base = -> Chamfer001
  Refine = true
  Tool = -> Extrude016
FEATURE [Part::Cut] Cut008  label="Lid Screw Hole"
  Base = -> Fusion012
  Placement = pos=(21,0,0) rot=(0,0,1;0rad)
  Refine = true
  Tool = -> Extrude015
FEATURE [Part::MultiFuse] Fusion013  label="Lid Screw Holes"
  Refine = true
  Shapes = -> [Cut008,Part__Feature101,Part__Feature102,Part__Feature103,Part__Feature104,Part__Feature105,Part__Feature106]
FEATURE [Part::MultiFuse] Fusion014
  Refine = true
  Shapes = -> [Cut007,Fusion013]
FEATURE [Sketcher::SketchObject] Sketch017
  FullyConstrained = false
  MapMode = 5
  Placement = pos=(70.4856,-106.261,0) rot=(0.919866,0.27735,0.27735;1.65423rad)
  Support = -> [Fusion014]
  sketch-geometry (4):
    g0: Circle CenterX=15 CenterY=27 CenterZ=0 NormalX=0 NormalY=0 NormalZ=1 AngleXU=0 Radius=2
    g1: Circle CenterX=15 CenterY=8 CenterZ=0 NormalX=0 NormalY=0 NormalZ=1 AngleXU=0 Radius=2
    g2: Circle CenterX=-15 CenterY=27 CenterZ=0 NormalX=0 NormalY=0 NormalZ=1 AngleXU=0 Radius=2
    g3: Circle CenterX=-15 CenterY=8 CenterZ=0 NormalX=0 NormalY=0 NormalZ=1 AngleXU=0 Radius=2
  constraints (9):
    c: Diameter(g1) = 4
    c: Diameter(g0) = 4
    c: DistanceX(g-2,g0) = 15
    c: DistanceX(g-2,g1) = 15
    c: Distance(g1,g0) = 19
    c: DistanceY(g-1,g1) = 8
    c: Diameter(g3) = 4
    c: Diameter(g2) = 4
    c: Distance(g3,g2) = 19
FEATURE [Part::Extrusion] Extrude017
  Base = -> Sketch017
  Dir = (0.552771,-0.833333,-5e-16)
  DirMode = 2
  FaceMakerClass = Part::FaceMakerBullseye
  LengthFwd = 10
  LengthRev = 0
  Solid = true
  Symmetric = true
FEATURE [Sketcher::SketchObject] Sketch018
  FullyConstrained = false
  MapMode = 5
  Placement = pos=(-70.4856,-106.261,0) rot=(0.919866,-0.27735,-0.27735;1.65423rad)
  Support = -> [Fusion014]
  sketch-geometry (4):
    g0: Circle CenterX=-15 CenterY=8 CenterZ=0 NormalX=0 NormalY=0 NormalZ=1 AngleXU=0 Radius=2
    g1: Circle CenterX=-15 CenterY=27 CenterZ=0 NormalX=0 NormalY=0 NormalZ=1 AngleXU=0 Radius=2
    g2: Circle CenterX=15 CenterY=8 CenterZ=0 NormalX=0 NormalY=0 NormalZ=1 AngleXU=0 Radius=2
    g3: Circle CenterX=15 CenterY=27 CenterZ=0 NormalX=0 NormalY=0 NormalZ=1 AngleXU=0 Radius=2
  constraints (9):
    c: Diameter(g1) = 4
    c: Distance(g1,g0) = 19
    c: DistanceY(g-1,g0) = 8
    c: DistanceX(g-2,g0) = -15
    c: DistanceX(g-2,g1) = -15
    c: Diameter(g0) = 4
    c: Diameter(g3) = 4
    c: Distance(g3,g2) = 19
    c: Diameter(g2) = 4
FEATURE [Part::Extrusion] Extrude018
  Base = -> Sketch018
  Dir = (-0.552771,-0.833333,0)
  DirMode = 2
  FaceMakerClass = Part::FaceMakerBullseye
  LengthFwd = 10
  LengthRev = 0
  Solid = true
  Symmetric = true
FEATURE [Sketcher::SketchObject] Sketch019
  FullyConstrained = false
  MapMode = 5
  Placement = pos=(0,-123.166,0) rot=(1,0,0;1.5708rad)
  Support = -> [Fusion014]
  sketch-geometry (4):
    g0: Circle CenterX=-25 CenterY=27 CenterZ=0 NormalX=0 NormalY=0 NormalZ=1 AngleXU=0 Radius=2
    g1: Circle CenterX=-25 CenterY=8 CenterZ=0 NormalX=0 NormalY=0 NormalZ=1 AngleXU=0 Radius=2
    g2: Circle CenterX=25 CenterY=27 CenterZ=0 NormalX=0 NormalY=0 NormalZ=1 AngleXU=0 Radius=2
    g3: Circle CenterX=25 CenterY=8 CenterZ=0 NormalX=0 NormalY=0 NormalZ=1 AngleXU=0 Radius=2
  constraints (9):
    c: Equal(g0,g1)
    c: Diameter(g0) = 4
    c: DistanceY(g-1,g1) = 8
    c: Distance(g1,g0) = 19
    c: DistanceX(g-2,g1) = -25
    c: DistanceX(g-2,g0) = -25
    c: Equal(g2,g3)
    c: Diameter(g2) = 4
    c: Distance(g3,g2) = 19
FEATURE [Part::Extrusion] Extrude019
  Base = -> Sketch019
  Dir = (0,-1,2e-16)
  DirMode = 2
  FaceMakerClass = Part::FaceMakerBullseye
  LengthFwd = 10
  LengthRev = 0
  Solid = true
  Symmetric = true
FEATURE [Part::MultiFuse] Fusion015  label="HitPlankScrewHoles"
  Refine = true
  Shapes = -> [Extrude018,Extrude019,Extrude017]
FEATURE [Part::Cut] Cut009  label="Robot Body"
  Base = -> Fusion014
  Refine = true
  Tool = -> Fusion015
FEATURE [Sketcher::SketchObject] Sketch020
  FullyConstrained = true
  MapMode = 5
  Placement = pos=(0,5.9e-15,26.7549) rot=(1,0,0;3.14159rad)
  Support = -> [Cut009]
  sketch-geometry (4):
    g0: LineSegment StartX=36 StartY=10 StartZ=0 EndX=56 EndY=10 EndZ=0
    g1: LineSegment StartX=56 StartY=10 StartZ=0 EndX=56 EndY=8 EndZ=0
    g2: LineSegment StartX=56 StartY=8 StartZ=0 EndX=36 EndY=8 EndZ=0
    g3: LineSegment StartX=36 StartY=8 StartZ=0 EndX=36 EndY=10 EndZ=0
  constraints (12):
    c: Coincident(g0,g1)
    c: Coincident(g1,g2)
    c: Coincident(g2,g3)
    c: Coincident(g3,g0)
    c: Horizontal(g0)
    c: Horizontal(g2)
    c: Vertical(g1)
    c: Vertical(g3)
    c: DistanceY(g-1,g1) = 8
    c: DistanceY(g1,g1) = 2
    c: DistanceX(g2,g2) = 20
    c: DistanceX(g-2,g2) = 36
FEATURE [Part::Extrusion] Extrude020  label="Motor Holders Lid Slot"
  Base = -> Sketch020
  Dir = (0,-2e-16,-1)
  DirMode = 2
  FaceMakerClass = Part::FaceMakerBullseye
  LengthFwd = 2
  LengthRev = 0
  Placement = pos=(0,1,0) rot=(0,0,1;0rad)
  Solid = true
  Symmetric = false
  TaperAngle = -3
FEATURE [Part::Extrusion] Extrude021  label="Motor Holders Lid Slot001"
  Base = -> Sketch020
  Dir = (0,-2e-16,-1)
  DirMode = 2
  FaceMakerClass = Part::FaceMakerBullseye
  LengthFwd = 2
  LengthRev = 0
  Placement = pos=(-92,17,0) rot=(0,0,1;0rad)
  Solid = true
  Symmetric = false
  TaperAngle = -3
FEATURE [Part::Extrusion] Extrude022  label="Motor Holders Lid Slot002"
  Base = -> Sketch020
  Dir = (0,-2e-16,-1)
  DirMode = 2
  FaceMakerClass = Part::FaceMakerBullseye
  LengthFwd = 2
  LengthRev = 0
  Placement = pos=(0,17,0) rot=(0,0,1;0rad)
  Solid = true
  Symmetric = false
  TaperAngle = -3
FEATURE [Part::Extrusion] Extrude023  label="Motor Holders Lid Slot003"
  Base = -> Sketch020
  Dir = (0,-2e-16,-1)
  DirMode = 2
  FaceMakerClass = Part::FaceMakerBullseye
  LengthFwd = 2
  LengthRev = 0
  Placement = pos=(-92,1,0) rot=(0,0,1;0rad)
  Solid = true
  Symmetric = false
  TaperAngle = -3
FEATURE [Part::MultiFuse] Fusion016  label="Motor Lid Gaps"
  Refine = true
  Shapes = -> [Extrude020,Extrude021,Extrude022,Extrude023]
FEATURE [Part::Cut] Cut010
  Base = -> Cut009
  Refine = true
  Tool = -> Fusion016
FEATURE [Sketcher::SketchObject] Sketch021
  FullyConstrained = true
  MapMode = 5
  Placement = pos=(0,2.25e-14,31.7549) rot=(1,0,0;3.14159rad)
  Support = -> [Cut010]
  sketch-geometry (8):
    g0: LineSegment StartX=-70 StartY=-44.9 StartZ=0 EndX=-25 EndY=-44.9 EndZ=0
    g1: LineSegment StartX=-25 StartY=-44.9 StartZ=0 EndX=-25 EndY=-63.3 EndZ=0
    g2: LineSegment StartX=-25 StartY=-63.3 StartZ=0 EndX=-70 EndY=-63.3 EndZ=0
    g3: LineSegment StartX=-70 StartY=-63.3 StartZ=0 EndX=-70 EndY=-44.9 EndZ=0
    g4: LineSegment StartX=-72 StartY=-42.9 StartZ=0 EndX=-23 EndY=-42.9 EndZ=0
    g5: LineSegment StartX=-23 StartY=-42.9 StartZ=0 EndX=-23 EndY=-65.3 EndZ=0
    g6: LineSegment StartX=-23 StartY=-65.3 StartZ=0 EndX=-72 EndY=-65.3 EndZ=0
    g7: LineSegment StartX=-72 StartY=-65.3 StartZ=0 EndX=-72 EndY=-42.9 EndZ=0
  constraints (24):
    c: Coincident(g0,g1)
    c: Coincident(g1,g2)
    c: Coincident(g2,g3)
    c: Coincident(g3,g0)
    c: Horizontal(g0)
    c: Horizontal(g2)
    c: Vertical(g1)
    c: Vertical(g3)
    c: Coincident(g4,g5)
    c: Coincident(g5,g6)
    c: Coincident(g6,g7)
    c: Coincident(g7,g4)
    c: Horizontal(g4)
    c: Horizontal(g6)
    c: Vertical(g5)
    c: Vertical(g7)
    c: Distance(g1,g5) = 2
    c: Distance(g1,g6) = 2
    c: Distance(g0,g4) = 2
    c: DistanceY(g-1,g0) = -44.9
    c: DistanceX(g-2,g0) = -25
    c: DistanceX(g0,g0) = 45
    c: DistanceY(g1,g1) = 18.4
    c: Distance(g0,g7) = 2
FEATURE [Part::Extrusion] Extrude024  label="Arduino Walls"
  Base = -> Sketch021
  Dir = (0,-7e-16,-1)
  DirMode = 2
  FaceMakerClass = Part::FaceMakerBullseye
  LengthFwd = 10
  LengthRev = 0
  Placement = pos=(0,-108,-19) rot=(0,0,1;0rad)
  Solid = true
  Symmetric = false
FEATURE [Part::MultiFuse] Fusion017  label="Full Robot Body"
  Refine = true
  Shapes = -> [Cut010,Extrude024]
FEATURE [Sketcher::SketchObject] Sketch024
  FullyConstrained = false
  MapMode = 5
  Placement = pos=(0,0,2) rot=(0,0,1;0rad)
  Support = -> [Fusion017]
  sketch-geometry (2):
    g0: Circle CenterX=15.0092 CenterY=-109.45 CenterZ=0 NormalX=0 NormalY=0 NormalZ=1 AngleXU=0 Radius=1.75
    g1: Circle CenterX=-15.0092 CenterY=-109.45 CenterZ=0 NormalX=0 NormalY=0 NormalZ=1 AngleXU=0 Radius=1.75
  constraints (2):
    c: Diameter(g0) = 3.5
    c: Diameter(g1) = 3.5
FEATURE [Part::Extrusion] Extrude025  label="Idle Wheel Base Screw Hole"
  Base = -> Sketch024
  Dir = (0,0,1)
  DirMode = 2
  FaceMakerClass = Part::FaceMakerBullseye
  LengthFwd = 10
  LengthRev = 0
  Solid = true
  Symmetric = true
FEATURE [Part::Cut] Cut011
  Base = -> Fusion017
  Refine = true
  Tool = -> Extrude025
FEATURE [Part::MultiFuse] Fusion018  label="Full Robot Body001"
  Refine = true
  Shapes = -> [Cut011,Extrude026]
FEATURE [Sketcher::SketchObject] Sketch025
  FullyConstrained = false
  MapMode = 5
  Placement = pos=(0,0,35) rot=(0,0,1;0rad)
  Support = -> [Fusion018]
  sketch-geometry (21):
    g0: LineSegment StartX=-59.987 StartY=34.8273 StartZ=0 EndX=59.8041 EndY=34.8273 EndZ=0
    g1: LineSegment StartX=59.8041 StartY=34.8273 StartZ=0 EndX=59.8041 EndY=-34.9668 EndZ=0
    g2: LineSegment StartX=59.8041 StartY=-34.9668 StartZ=0 EndX=94.9993 EndY=-34.9668 EndZ=0
    g3: LineSegment StartX=94.9993 StartY=-34.9668 StartZ=0 EndX=94.9993 EndY=-89.9973 EndZ=0
    g4: LineSegment StartX=94.9993 StartY=-89.9973 StartZ=0 EndX=44.9644 EndY=-123.178 EndZ=0
    g5: LineSegment StartX=44.9644 StartY=-123.178 StartZ=0 EndX=-45.0068 EndY=-123.178 EndZ=0
    g6: LineSegment StartX=-45.0068 StartY=-123.178 StartZ=0 EndX=-94.9992 EndY=-90.0114 EndZ=0
    g7: LineSegment StartX=-94.9992 StartY=-90.0114 StartZ=0 EndX=-94.9992 EndY=-35.0079 EndZ=0
    g8: LineSegment StartX=-94.9992 StartY=-35.0079 StartZ=0 EndX=-59.987 EndY=-35.0079 EndZ=0
    g9: LineSegment StartX=-59.987 StartY=-35.0079 StartZ=0 EndX=-59.987 EndY=34.8273 EndZ=0
    g10: LineSegment StartX=-9.99147 StartY=-91.5603 StartZ=0 EndX=10.0409 EndY=-91.5603 EndZ=0
    g11: LineSegment StartX=10.0409 StartY=-91.5603 StartZ=0 EndX=10.0409 EndY=-95.508 EndZ=0
    g12: LineSegment StartX=10.0409 StartY=-95.508 StartZ=0 EndX=-9.99147 EndY=-95.508 EndZ=0
    g13: LineSegment StartX=-9.99147 StartY=-95.508 StartZ=0 EndX=-9.99147 EndY=-91.5603 EndZ=0
    g14: Circle CenterX=37.419 CenterY=29.3 CenterZ=0 NormalX=0 NormalY=0 NormalZ=1 AngleXU=0 Radius=1.5
    g15: Circle CenterX=-37.6122 CenterY=29.279 CenterZ=0 NormalX=0 NormalY=0 NormalZ=1 AngleXU=0 Radius=1.5
    g16: Circle CenterX=-0.59146 CenterY=-34.6907 CenterZ=0 NormalX=0 NormalY=0 NormalZ=1 AngleXU=0 Radius=1.5
    g17: Circle CenterX=70.9045 CenterY=-39.7106 CenterZ=0 NormalX=0 NormalY=0 NormalZ=1 AngleXU=0 Radius=1.5
    g18: Circle CenterX=30.5752 CenterY=-118.304 CenterZ=0 NormalX=0 NormalY=0 NormalZ=1 AngleXU=0 Radius=1.5
    g19: Circle CenterX=-31.3681 CenterY=-118.305 CenterZ=0 NormalX=0 NormalY=0 NormalZ=1 AngleXU=0 Radius=1.5
    g20: Circle CenterX=-67.5923 CenterY=-39.7098 CenterZ=0 NormalX=0 NormalY=0 NormalZ=1 AngleXU=0 Radius=1.5
  constraints (33):
    c: Horizontal(g0)
    c: Coincident(g0,g1)
    c: Vertical(g1)
    c: Coincident(g1,g2)
    c: Horizontal(g2)
    c: Coincident(g2,g3)
    c: Vertical(g3)
    c: Coincident(g3,g4)
    c: Coincident(g4,g5)
    c: Horizontal(g5)
    c: Coincident(g5,g6)
    c: Coincident(g6,g7)
    c: Vertical(g7)
    c: Coincident(g7,g8)
    c: Horizontal(g8)
    c: Coincident(g8,g9)
    c: Coincident(g9,g0)
    c: Vertical(g9)
    c: Coincident(g10,g11)
    c: Coincident(g11,g12)
    c: Coincident(g12,g13)
    c: Coincident(g13,g10)
    c: Horizontal(g10)
    c: Horizontal(g12)
    c: Vertical(g11)
    c: Vertical(g13)
    c: Diameter(g14) = 3
    c: Diameter(g15) = 3
    c: Diameter(g16) = 3
    c: Diameter(g17) = 3
    c: Diameter(g18) = 3
    c: Diameter(g19) = 3
    c: Diameter(g20) = 3
FEATURE [Part::Extrusion] Extrude027  label="Lid Base"
  Base = -> Sketch025
  Dir = (0,0,1)
  DirMode = 2
  FaceMakerClass = Part::FaceMakerBullseye
  LengthFwd = 3
  LengthRev = 0
  Solid = true
  Symmetric = false
FEATURE [Part::Fillet] Fillet
  Base = -> Extrude027
  Edges = 21 edges r=1: [Edge4,Edge7,Edge10,Edge13,Edge16,Edge19,Edge22,Edge25,Edge28,Edge30,Edge34,Edge37,Edge40,Edge42,Edge45,Edge48,Edge51,Edge54,Edge57,Edge60,Edge63]
FEATURE [Sketcher::SketchObject] Sketch026
  FullyConstrained = true
  MapMode = 5
  Placement = pos=(0,0,38) rot=(0,0,1;0rad)
  Support = -> [Fillet]
  sketch-geometry (1):
    g0: Circle CenterX=0 CenterY=-110 CenterZ=0 NormalX=0 NormalY=0 NormalZ=1 AngleXU=0 Radius=2
  constraints (3):
    c: Diameter(g0) = 4
    c: DistanceY(g0,g-1) = 110
    c: PointOnObject(g0,g-2)
FEATURE [Part::Extrusion] Extrude028  label="Weapon Wire slot"
  Base = -> Sketch026
  Dir = (0,0,1)
  DirMode = 2
  FaceMakerClass = Part::FaceMakerBullseye
  LengthFwd = 10
  LengthRev = 0
  Placement = pos=(-27,0,-6.5) rot=(0,0,1;0rad)
  Solid = true
  Symmetric = false
FEATURE [Part::Cut] Cut012
  Base = -> Fillet
  Refine = true
  Tool = -> Extrude028
FEATURE [Sketcher::SketchObject] Sketch028
  FullyConstrained = true
  MapMode = 5
  Placement = pos=(0,0,38) rot=(0,0,1;0rad)
  Support = -> [Cut012]
  sketch-geometry (9):
    g0: LineSegment StartX=-17 StartY=-100 StartZ=0 EndX=0 EndY=-100 EndZ=0
    g1: LineSegment StartX=0 StartY=-100 StartZ=0 EndX=0 EndY=-102 EndZ=0
    g2: LineSegment StartX=0 StartY=-102 StartZ=0 EndX=-17 EndY=-102 EndZ=0
    g3: LineSegment StartX=-17 StartY=-102 StartZ=0 EndX=-17 EndY=-100 EndZ=0
    g4: LineSegment StartX=-17 StartY=-118 StartZ=0 EndX=0 EndY=-118 EndZ=0
    g5: LineSegment StartX=0 StartY=-118 StartZ=0 EndX=0 EndY=-120 EndZ=0
    g6: LineSegment StartX=0 StartY=-120 StartZ=0 EndX=-17 EndY=-120 EndZ=0
    g7: LineSegment StartX=-17 StartY=-120 StartZ=0 EndX=-17 EndY=-118 EndZ=0
    g8: LineSegment StartX=0 StartY=-102 StartZ=0 EndX=0 EndY=-118 EndZ=0
  constraints (26):
    c: Coincident(g0,g1)
    c: Coincident(g1,g2)
    c: Coincident(g2,g3)
    c: Coincident(g3,g0)
    c: Horizontal(g2)
    c: Vertical(g1)
    c: Vertical(g3)
    c: Coincident(g4,g5)
    c: Coincident(g5,g6)
    c: Coincident(g6,g7)
    c: Coincident(g7,g4)
    c: Horizontal(g4)
    c: Horizontal(g6)
    c: Vertical(g5)
    c: Vertical(g7)
    c: Distance(g1,g4) = 16
    c: Distance(g-1,g0) = 100
    c: DistanceX(g0,g0) = 17
    c: DistanceY(g3,g3) = 2
    c: DistanceY(g5,g5) = 2
    c: DistanceX(g6,g6) = 17
    c: Coincident(g8,g1)
    c: Coincident(g8,g4)
    c: Vertical(g8)
    c: DistanceY(g1,g1) = 2
    c: PointOnObject(g0,g-2)
FEATURE [Part::Extrusion] Extrude029  label="Motor Flange Gap"
  Base = -> Sketch028
  Dir = (0,0,1)
  DirMode = 2
  FaceMakerClass = Part::FaceMakerBullseye
  LengthFwd = 10
  LengthRev = 0
  Solid = true
  Symmetric = true
FEATURE [Part::Cut] Cut013
  Base = -> Cut012
  Refine = true
  Tool = -> Extrude029
FEATURE [Part::Box] Box008  label="Cubo006"
  AttacherType = Attacher::AttachEngine3D
  Height = 35
  Length = 186
  Placement = pos=(-93,-147,1) rot=(0,0,1;0rad)
  Width = 4
FEATURE [Part::Box] Box009  label="Cubo007"
  AttacherType = Attacher::AttachEngine3D
  Height = 40
  Length = 200
  Placement = pos=(-100,-140,-4) rot=(0,0,1;0rad)
  Width = 50
FEATURE [Part::Cut] Cut015
  Base = -> Fusion018
  Tool = -> Box009
FEATURE [Sketcher::SketchObject] Sketch036
  FullyConstrained = false
  sketch-geometry (2):
    g0: ArcOfCircle CenterX=0.0180278 CenterY=37.967 CenterZ=0 NormalX=0 NormalY=0 NormalZ=1 AngleXU=0 Radius=158.19 StartAngle=4.08404 EndAngle=5.34074
    g1: LineSegment StartX=-92.9675 StartY=-90.0081 StartZ=0 EndX=93.0036 EndY=-90.0081 EndZ=0
  constraints (3):
    c: Coincident(g1,g0)
    c: Coincident(g1,g0)
    c: Horizontal(g1)
FEATURE [Part::Extrusion] Extrude034
  Base = -> Sketch036
  Dir = (0,0,1)
  DirMode = 2
  FaceMakerClass = Part::FaceMakerBullseye
  LengthFwd = 35
  LengthRev = 0
  Solid = true
  Symmetric = false
FEATURE [Part::Thickness] Thickness003
  Faces = -> Extrude034 [Face4]
  Intersection = false
  Join = 0
  Mode = 0
  Placement = pos=(0,-56,0) rot=(0,0,1;0rad)
  SelfIntersection = false
  Value = 2
FEATURE [Part::Cut] Cut
  Base = -> Thickness003
  Placement = pos=(0,56,2) rot=(0,0,1;0rad)
  Tool = -> Box008
FEATURE [Part::Box] Box  label="Cubo"
  AttacherType = Attacher::AttachEngine3D
  Height = 2
  Length = 200
  Placement = pos=(-101,-136,35) rot=(0,0,1;0rad)
  Width = 60
FEATURE [Part::Cut] Cut016
  Base = -> Cut
  Tool = -> Box
FEATURE [Part::Feature] Part__Feature046  label="Robot Rim"
  shape: bbox 40 x 40 x 20.01 mm, 43 faces (baked)
FEATURE [Part::Feature] Part__Feature047  label="Robot Slick Tire"
  Placement = pos=(0,0,10) rot=(0,0,1;0rad)
  shape: bbox 45 x 45 x 15 mm, 4 faces (baked)
FEATURE [App::Part] robot  label="LeftTire"
  Group = -> [Part__Feature046,Part__Feature047]
  Origin = -> Origin002
  Placement = pos=(61.5,0,7) rot=(0,1,0;1.5708rad)
FEATURE [Part::Feature] Part__Feature048  label="Robot Rim001"
  shape: bbox 40 x 40 x 20.01 mm, 43 faces (baked)
FEATURE [Part::Feature] Part__Feature049  label="Robot Slick Tire001"
  Placement = pos=(0,0,10) rot=(0,0,1;0rad)
  shape: bbox 45 x 45 x 15 mm, 4 faces (baked)
FEATURE [App::Part] robot001  label="RightTire"
  Group = -> [Part__Feature048,Part__Feature049]
  Origin = -> Origin003
  Placement = pos=(-62,0,7) rot=(0,1,0;4.71239rad)
FEATURE [Part::Feature] Part__Feature  label="L298N"
  Placement = pos=(21.5,29,6) rot=(1,0,0;1.5708rad)
  shape: bbox 43 x 43 x 25 mm, 410 faces (baked)
FEATURE [Part::Feature] Part__Feature001  label="Motor Case"
  shape: bbox 14 x 10 x 12 mm, 26 faces (baked)
FEATURE [Part::Feature] Part__Feature002  label="Rear Cover"
  Placement = pos=(7,0,0) rot=(0,0,1;0rad)
  shape: bbox 9 x 10 x 12 mm, 45 faces (baked)
FEATURE [Part::Feature] Part__Feature003  label="Rear Bearing"
  Placement = pos=(8.5,0,0) rot=(1,0,0;0.268142rad)
  shape: bbox 3 x 5 x 5 mm, 9 faces (baked)
FEATURE [Part::Feature] Part__Feature004  label="Front Bearing"
  Placement = pos=(-5.5,-1e-15,0) rot=(0,0,1;0rad)
  shape: bbox 1.5 x 4 x 4 mm, 6 faces (baked)
FEATURE [Part::Feature] Part__Feature005  label="Rotor"
  Placement = pos=(7,-3e-15,0) rot=(1,0,0;0.383419rad)
  shape: bbox 16.7 x 7.6 x 7.6 mm, 34 faces, 3 solids (baked)
FEATURE [Part::Feature] Part__Feature006  label="Spur 1-15_Spur01"
  Placement = pos=(-8.95,-3e-15,0) rot=(0.012886,0.999834,0.012886;1.57096rad)
  shape: bbox 1.5 x 3.391 x 3.382 mm, 38 faces (baked)
FEATURE [Part::Feature] Part__Feature007  label="Plate 1"
  Placement = pos=(-8,-6e-15,6e-15) rot=(0,1,0;1.5708rad)
  shape: bbox 1 x 10 x 12 mm, 14 faces (baked)
FEATURE [Part::Feature] Part__Feature008  label="Stand 2"
  Placement = pos=(-10,3.2,-3.6) rot=(0,0,1;0rad)
  shape: bbox 2 x 3 x 3 mm, 6 faces (baked)
FEATURE [Part::Feature] Part__Feature009  label="Stand 003"
  Placement = pos=(-10,-3.2,3.6) rot=(0,0,1;0rad)
  shape: bbox 2 x 3 x 3 mm, 6 faces (baked)
FEATURE [Part::Feature] Part__Feature010  label="Spur 2-24_Spur01"
  Placement = pos=(-8.95,2.21201,3.21201) rot=(0.153612,-0.976118,-0.153612;1.59497rad)
  shape: bbox 10.4 x 5.193 x 5.193 mm, 56 faces (baked)
FEATURE [Part::Feature] Part__Feature011  label="Plate 2"
  Placement = pos=(-11,-1.9e-14,5e-15) rot=(0,1,0;1.5708rad)
  shape: bbox 1 x 10 x 12 mm, 17 faces (baked)
FEATURE [Part::Feature] Part__Feature012  label="Spur 2-15_Spur01"
  Placement = pos=(-11.2,2.21201,3.21201) rot=(0.392285,0.832,0.392285;1.75369rad)
  shape: bbox 3 x 3.389 x 3.386 mm, 34 faces (baked)
FEATURE [Part::Feature] Part__Feature013  label="Spur 1-26_Spur01"
  Placement = pos=(-11.95,-0.153707,-0.136628) rot=(-0.467826,-0.749852,0.467826;1.85478rad)
  shape: bbox 4.2 x 5.587 x 5.6 mm, 60 faces (baked)
FEATURE [Part::Feature] Part__Feature014  label="Spur 1-15_Spur002"
  Placement = pos=(-13.45,-0.153707,-0.136628) rot=(-0.575214,0.581599,-0.575214;2.08803rad)
  shape: bbox 1.5 x 3.378 x 3.392 mm, 38 faces (baked)
FEATURE [Part::Feature] Part__Feature015  label="Stand 4"
  Placement = pos=(-16.1,3.2,-3.6) rot=(-1,0,0;1.00084rad)
  shape: bbox 5.1 x 3 x 3 mm, 6 faces (baked)
FEATURE [Part::Feature] Part__Feature016  label="Stand 004"
  Placement = pos=(-16.1,-3.2,3.6) rot=(1,0,0;1.52971rad)
  shape: bbox 5.1 x 3 x 3 mm, 6 faces (baked)
FEATURE [Part::Feature] Part__Feature017  label="Spur 1-24_Spur01"
  Placement = pos=(-13.45,-2.35559,-3.35559) rot=(-0.550538,0.627547,-0.550538;2.02074rad)
  shape: bbox 7.1 x 5.2 x 5.2 mm, 56 faces (baked)
FEATURE [Part::Feature] Part__Feature018  label="Plate 3"
  Placement = pos=(-16.1,-2.1e-14,5e-15) rot=(0.707107,0,-0.707107;3.14159rad)
  shape: bbox 2 x 10.2 x 12 mm, 29 faces (baked)
FEATURE [Part::Feature] Part__Feature019  label="Spur 1-15_Spur003"
  Placement = pos=(-15.15,-2.35559,-3.35559) rot=(0.659293,0.361476,0.659293;2.44787rad)
  shape: bbox 1.5 x 3.389 x 3.386 mm, 38 faces (baked)
FEATURE [Part::Feature] Part__Feature020  label="Spur 2-26_Spur01"
  Placement = pos=(-15.15,-2.7e-14,5e-15) rot=(0.080265,0.993537,0.080265;1.57728rad)
  shape: bbox 11.5 x 5.592 x 5.599 mm, 59 faces (baked)
FEATURE [Part::Feature] Part__Feature021  label="countersunk flat head cross recess screw_iso_ISO 7046-1 - M2 x 12 - Z --- 12N"
  Placement = pos=(-17.4,-3.2,3.6) rot=(1,0,0;0.036509rad)
  shape: bbox 12 x 3.8 x 3.8 mm, 41 faces (baked)
FEATURE [Part::Feature] Part__Feature022  label="countersunk flat head cross recess screw_iso_ISO 7046-1 - M2 x 12 - Z --- 12N001"
  Placement = pos=(-17.4,3.2,-3.6) rot=(1,0,0;1.44457rad)
  shape: bbox 12 x 3.8 x 3.8 mm, 41 faces (baked)
FEATURE [App::Part] GA12_N20_Motor_Complet  label="Left Motor"
  Group = -> [Part__Feature001,Part__Feature002,Part__Feature003,Part__Feature004,Part__Feature005,Part__Feature006,Part__Feature007,Part__Feature008,Part__Feature009,Part__Feature010,Part__Feature011,Part__Feature012,Part__Feature013,Part__Feature014,Part__Feature015,Part__Feature016,Part__Feature017,Part__Feature018,Part__Feature019,Part__Feature020,Part__Feature021,Part__Feature022]
  Origin = -> Origin
  Placement = pos=(40,-7.2e-15,7) rot=(0,0.707107,0.707107;3.14159rad)
FEATURE [Part::Feature] Part__Feature107  label="Motor Case001"
  shape: bbox 14 x 10 x 12 mm, 26 faces (baked)
FEATURE [Part::Feature] Part__Feature108  label="Rear Cover001"
  Placement = pos=(7,0,0) rot=(0,0,1;0rad)
  shape: bbox 9 x 10 x 12 mm, 45 faces (baked)
FEATURE [Part::Feature] Part__Feature109  label="Rear Bearing001"
  Placement = pos=(8.5,0,0) rot=(1,0,0;0.268142rad)
  shape: bbox 3 x 5 x 5 mm, 9 faces (baked)
FEATURE [Part::Feature] Part__Feature110  label="Front Bearing001"
  Placement = pos=(-5.5,-1e-15,0) rot=(0,0,1;0rad)
  shape: bbox 1.5 x 4 x 4 mm, 6 faces (baked)
FEATURE [Part::Feature] Part__Feature111  label="Rotor001"
  Placement = pos=(7,-3e-15,0) rot=(1,0,0;0.383419rad)
  shape: bbox 16.7 x 7.6 x 7.6 mm, 34 faces, 3 solids (baked)
FEATURE [Part::Feature] Part__Feature112  label="Spur 1-15_Spur004"
  Placement = pos=(-8.95,-3e-15,0) rot=(0.012886,0.999834,0.012886;1.57096rad)
  shape: bbox 1.5 x 3.391 x 3.382 mm, 38 faces (baked)
FEATURE [Part::Feature] Part__Feature113  label="Plate 004"
  Placement = pos=(-8,-6e-15,6e-15) rot=(0,1,0;1.5708rad)
  shape: bbox 1 x 10 x 12 mm, 14 faces (baked)
FEATURE [Part::Feature] Part__Feature114  label="Stand 005"
  Placement = pos=(-10,3.2,-3.6) rot=(0,0,1;0rad)
  shape: bbox 2 x 3 x 3 mm, 6 faces (baked)
FEATURE [Part::Feature] Part__Feature115  label="Stand 006"
  Placement = pos=(-10,-3.2,3.6) rot=(0,0,1;0rad)
  shape: bbox 2 x 3 x 3 mm, 6 faces (baked)
FEATURE [Part::Feature] Part__Feature116  label="Spur 2-24_Spur002"
  Placement = pos=(-8.95,2.21201,3.21201) rot=(0.153612,-0.976118,-0.153612;1.59497rad)
  shape: bbox 10.4 x 5.193 x 5.193 mm, 56 faces (baked)
FEATURE [Part::Feature] Part__Feature117  label="Plate 005"
  Placement = pos=(-11,-1.9e-14,5e-15) rot=(0,1,0;1.5708rad)
  shape: bbox 1 x 10 x 12 mm, 17 faces (baked)
FEATURE [Part::Feature] Part__Feature118  label="Spur 2-15_Spur002"
  Placement = pos=(-11.2,2.21201,3.21201) rot=(0.392285,0.832,0.392285;1.75369rad)
  shape: bbox 3 x 3.389 x 3.386 mm, 34 faces (baked)
FEATURE [Part::Feature] Part__Feature119  label="Spur 1-26_Spur002"
  Placement = pos=(-11.95,-0.153707,-0.136628) rot=(-0.467826,-0.749852,0.467826;1.85478rad)
  shape: bbox 4.2 x 5.587 x 5.6 mm, 60 faces (baked)
FEATURE [Part::Feature] Part__Feature120  label="Spur 1-15_Spur005"
  Placement = pos=(-13.45,-0.153707,-0.136628) rot=(-0.575214,0.581599,-0.575214;2.08803rad)
  shape: bbox 1.5 x 3.378 x 3.392 mm, 38 faces (baked)
FEATURE [Part::Feature] Part__Feature121  label="Stand 007"
  Placement = pos=(-16.1,3.2,-3.6) rot=(-1,0,0;1.00084rad)
  shape: bbox 5.1 x 3 x 3 mm, 6 faces (baked)
FEATURE [Part::Feature] Part__Feature122  label="Stand 008"
  Placement = pos=(-16.1,-3.2,3.6) rot=(1,0,0;1.52971rad)
  shape: bbox 5.1 x 3 x 3 mm, 6 faces (baked)
FEATURE [Part::Feature] Part__Feature123  label="Spur 1-24_Spur002"
  Placement = pos=(-13.45,-2.35559,-3.35559) rot=(-0.550538,0.627547,-0.550538;2.02074rad)
  shape: bbox 7.1 x 5.2 x 5.2 mm, 56 faces (baked)
FEATURE [Part::Feature] Part__Feature124  label="Plate 006"
  Placement = pos=(-16.1,-2.1e-14,5e-15) rot=(0.707107,0,-0.707107;3.14159rad)
  shape: bbox 2 x 10.2 x 12 mm, 29 faces (baked)
FEATURE [Part::Feature] Part__Feature125  label="Spur 1-15_Spur006"
  Placement = pos=(-15.15,-2.35559,-3.35559) rot=(0.659293,0.361476,0.659293;2.44787rad)
  shape: bbox 1.5 x 3.389 x 3.386 mm, 38 faces (baked)
FEATURE [Part::Feature] Part__Feature126  label="Spur 2-26_Spur002"
  Placement = pos=(-15.15,-2.7e-14,5e-15) rot=(0.080265,0.993537,0.080265;1.57728rad)
  shape: bbox 11.5 x 5.592 x 5.599 mm, 59 faces (baked)
FEATURE [Part::Feature] Part__Feature127  label="countersunk flat head cross recess screw_iso_ISO 7046-1 - M2 x 12 - Z --- 12N002"
  Placement = pos=(-17.4,-3.2,3.6) rot=(1,0,0;0.036509rad)
  shape: bbox 12 x 3.8 x 3.8 mm, 41 faces (baked)
FEATURE [Part::Feature] Part__Feature128  label="countersunk flat head cross recess screw_iso_ISO 7046-1 - M2 x 12 - Z --- 12N003"
  Placement = pos=(-17.4,3.2,-3.6) rot=(1,0,0;1.44457rad)
  shape: bbox 12 x 3.8 x 3.8 mm, 41 faces (baked)
FEATURE [App::Part] GA12_N20_Motor_Complet001  label="Left Motor001"
  Group = -> [Part__Feature107,Part__Feature108,Part__Feature109,Part__Feature110,Part__Feature111,Part__Feature112,Part__Feature113,Part__Feature114,Part__Feature115,Part__Feature116,Part__Feature117,Part__Feature118,Part__Feature119,Part__Feature120,Part__Feature121,Part__Feature122,Part__Feature123,Part__Feature124,Part__Feature125,Part__Feature126,Part__Feature127,Part__Feature128]
  Origin = -> Origin004
  Placement = pos=(40,-7.2e-15,7) rot=(0,0.707107,0.707107;3.14159rad)
FEATURE [Part::Feature] Part__Feature023  label="Motor Case002"
  shape: bbox 14 x 10 x 12 mm, 26 faces (baked)
FEATURE [Part::Feature] Part__Feature024  label="Rear Cover002"
  Placement = pos=(7,0,0) rot=(0,0,1;0rad)
  shape: bbox 9 x 10 x 12 mm, 45 faces (baked)
FEATURE [Part::Feature] Part__Feature025  label="Rear Bearing002"
  Placement = pos=(8.5,0,0) rot=(1,0,0;0.268142rad)
  shape: bbox 3 x 5 x 5 mm, 9 faces (baked)
FEATURE [Part::Feature] Part__Feature026  label="Front Bearing002"
  Placement = pos=(-5.5,-1e-15,0) rot=(0,0,1;0rad)
  shape: bbox 1.5 x 4 x 4 mm, 6 faces (baked)
FEATURE [Part::Feature] Part__Feature027  label="Rotor002"
  Placement = pos=(7,-3e-15,0) rot=(1,0,0;0.383419rad)
  shape: bbox 16.7 x 7.6 x 7.6 mm, 34 faces, 3 solids (baked)
FEATURE [Part::Feature] Part__Feature028  label="Spur 1-15_Spur007"
  Placement = pos=(-8.95,-3e-15,0) rot=(0.012886,0.999834,0.012886;1.57096rad)
  shape: bbox 1.5 x 3.391 x 3.382 mm, 38 faces (baked)
FEATURE [Part::Feature] Part__Feature029  label="Plate 007"
  Placement = pos=(-8,-6e-15,6e-15) rot=(0,1,0;1.5708rad)
  shape: bbox 1 x 10 x 12 mm, 14 faces (baked)
FEATURE [Part::Feature] Part__Feature030  label="Stand 009"
  Placement = pos=(-10,3.2,-3.6) rot=(0,0,1;0rad)
  shape: bbox 2 x 3 x 3 mm, 6 faces (baked)
FEATURE [Part::Feature] Part__Feature031  label="Stand 010"
  Placement = pos=(-10,-3.2,3.6) rot=(0,0,1;0rad)
  shape: bbox 2 x 3 x 3 mm, 6 faces (baked)
FEATURE [Part::Feature] Part__Feature032  label="Spur 2-24_Spur003"
  Placement = pos=(-8.95,2.21201,3.21201) rot=(0.153612,-0.976118,-0.153612;1.59497rad)
  shape: bbox 10.4 x 5.193 x 5.193 mm, 56 faces (baked)
FEATURE [Part::Feature] Part__Feature033  label="Plate 008"
  Placement = pos=(-11,-1.9e-14,5e-15) rot=(0,1,0;1.5708rad)
  shape: bbox 1 x 10 x 12 mm, 17 faces (baked)
FEATURE [Part::Feature] Part__Feature034  label="Spur 2-15_Spur003"
  Placement = pos=(-11.2,2.21201,3.21201) rot=(0.392285,0.832,0.392285;1.75369rad)
  shape: bbox 3 x 3.389 x 3.386 mm, 34 faces (baked)
FEATURE [Part::Feature] Part__Feature035  label="Spur 1-26_Spur003"
  Placement = pos=(-11.95,-0.153707,-0.136628) rot=(-0.467826,-0.749852,0.467826;1.85478rad)
  shape: bbox 4.2 x 5.587 x 5.6 mm, 60 faces (baked)
FEATURE [Part::Feature] Part__Feature036  label="Spur 1-15_Spur008"
  Placement = pos=(-13.45,-0.153707,-0.136628) rot=(-0.575214,0.581599,-0.575214;2.08803rad)
  shape: bbox 1.5 x 3.378 x 3.392 mm, 38 faces (baked)
FEATURE [Part::Feature] Part__Feature037  label="Stand 011"
  Placement = pos=(-16.1,3.2,-3.6) rot=(-1,0,0;1.00084rad)
  shape: bbox 5.1 x 3 x 3 mm, 6 faces (baked)
FEATURE [Part::Feature] Part__Feature038  label="Stand 012"
  Placement = pos=(-16.1,-3.2,3.6) rot=(1,0,0;1.52971rad)
  shape: bbox 5.1 x 3 x 3 mm, 6 faces (baked)
FEATURE [Part::Feature] Part__Feature039  label="Spur 1-24_Spur003"
  Placement = pos=(-13.45,-2.35559,-3.35559) rot=(-0.550538,0.627547,-0.550538;2.02074rad)
  shape: bbox 7.1 x 5.2 x 5.2 mm, 56 faces (baked)
FEATURE [Part::Feature] Part__Feature040  label="Plate 009"
  Placement = pos=(-16.1,-2.1e-14,5e-15) rot=(0.707107,0,-0.707107;3.14159rad)
  shape: bbox 2 x 10.2 x 12 mm, 29 faces (baked)
FEATURE [Part::Feature] Part__Feature041  label="Spur 1-15_Spur009"
  Placement = pos=(-15.15,-2.35559,-3.35559) rot=(0.659293,0.361476,0.659293;2.44787rad)
  shape: bbox 1.5 x 3.389 x 3.386 mm, 38 faces (baked)
FEATURE [Part::Feature] Part__Feature042  label="Spur 2-26_Spur003"
  Placement = pos=(-15.15,-2.7e-14,5e-15) rot=(0.080265,0.993537,0.080265;1.57728rad)
  shape: bbox 11.5 x 5.592 x 5.599 mm, 59 faces (baked)
FEATURE [Part::Feature] Part__Feature043  label="countersunk flat head cross recess screw_iso_ISO 7046-1 - M2 x 12 - Z --- 12N004"
  Placement = pos=(-17.4,-3.2,3.6) rot=(1,0,0;0.036509rad)
  shape: bbox 12 x 3.8 x 3.8 mm, 41 faces (baked)
FEATURE [Part::Feature] Part__Feature044  label="countersunk flat head cross recess screw_iso_ISO 7046-1 - M2 x 12 - Z --- 12N005"
  Placement = pos=(-17.4,3.2,-3.6) rot=(1,0,0;1.44457rad)
  shape: bbox 12 x 3.8 x 3.8 mm, 41 faces (baked)
FEATURE [App::Part] GA12_N20_Motor_Complet002  label="Right Motor"
  Group = -> [Part__Feature023,Part__Feature024,Part__Feature025,Part__Feature026,Part__Feature027,Part__Feature028,Part__Feature029,Part__Feature030,Part__Feature031,Part__Feature032,Part__Feature033,Part__Feature034,Part__Feature035,Part__Feature036,Part__Feature037,Part__Feature038,Part__Feature039,Part__Feature040,Part__Feature041,Part__Feature042,Part__Feature043,Part__Feature044]
  Origin = -> Origin001
  Placement = pos=(-40,-1.5e-14,7) rot=(1,0,0;1.5708rad)
FEATURE [Part::Feature] Part__Feature051  label="Arduino Nano"
  Placement = pos=(8.85506,11.9484,3.8e-15) rot=(0,0,1;0rad)
  shape: bbox 43.18 x 18 x 6.8 mm, 962 faces (baked)
FEATURE [Part::Feature] Part__Feature052  label="Mini USB"
  Placement = pos=(8.54506,19.5727,4.14) rot=(0,0,1;0rad)
  shape: bbox 9.5 x 9.7 x 3.9 mm, 197 faces (baked)
FEATURE [Part::Feature] Part__Feature053  label="ATMEGA328P-AU--3DModel-STEP-56544.step.STEP.STEP.STEP"
  Placement = pos=(2.81625,4.09996,0.676804) rot=(1,0,0;1.5708rad)
  shape: bbox 9 x 9 x 1.2 mm, 650 faces, 33 solids (baked)
FEATURE [App::Part] ATMEGA328P_AU_STEP  label="ATMEGA328P-AU.STEP"
  Group = -> [Part__Feature053]
  Origin = -> Origin005
  Placement = pos=(19.8219,24.4243,4.0882) rot=(0,0,1;3.92699rad)
FEATURE [Part::Feature] Part__Feature054  label="CSTCE Crystal"
  Placement = pos=(25.8562,23.1047,4.15) rot=(0,0,-1;0.785398rad)
  shape: bbox 3.182 x 3.182 x 0.71 mm, 47 faces (baked)
FEATURE [Part::Feature] Part__Feature055  label="2Pin Tactile Switch 6x3.6"
  Placement = pos=(30.7142,19.8184,4.14) rot=(0,0,1;1.5708rad)
  shape: bbox 3.633 x 7.9 x 2.2 mm, 48 faces (baked)
FEATURE [Part::Feature] Part__Feature056  label="0603 Resistor"
  Placement = pos=(34.4251,22.4184,4.14) rot=(0,0,1;0rad)
  shape: bbox 1.6 x 0.8 x 0.5 mm, 69 faces (baked)
FEATURE [Part::Feature] Part__Feature057  label="0603 Resistor001"
  Placement = pos=(34.4251,20.7184,4.14) rot=(0,0,1;0rad)
  shape: bbox 1.6 x 0.8 x 0.5 mm, 69 faces (baked)
FEATURE [Part::Feature] Part__Feature058  label="0603 Resistor002"
  Placement = pos=(34.4251,18.9184,4.14) rot=(0,0,1;0rad)
  shape: bbox 1.6 x 0.8 x 0.5 mm, 69 faces (baked)
FEATURE [Part::Feature] Part__Feature059  label="0603 Resistor003"
  Placement = pos=(34.4251,17.2184,4.14) rot=(0,0,1;0rad)
  shape: bbox 1.6 x 0.8 x 0.5 mm, 69 faces (baked)
FEATURE [Part::Feature] Part__Feature060  label="Blue LED"
  Placement = pos=(37.0251,22.4184,4.14) rot=(0,0,1;0rad)
  shape: bbox 1.6 x 0.8 x 0.6 mm, 19 faces (baked)
FEATURE [Part::Feature] Part__Feature061  label="Green LED"
  Placement = pos=(37.0251,20.7184,4.14) rot=(0,0,1;0rad)
  shape: bbox 1.6 x 0.8 x 0.6 mm, 19 faces (baked)
FEATURE [Part::Feature] Part__Feature062  label="Red LED"
  Placement = pos=(37.0251,18.9184,4.14) rot=(0,0,1;0rad)
  shape: bbox 1.6 x 0.8 x 0.6 mm, 19 faces (baked)
FEATURE [Part::Feature] Part__Feature063  label="Blue LED001"
  Placement = pos=(37.0251,17.2184,4.14) rot=(0,0,1;0rad)
  shape: bbox 1.6 x 0.8 x 0.6 mm, 19 faces (baked)
FEATURE [Part::Feature] Part__Feature064  label="Header 2x3"
  Placement = pos=(45.6765,17.0321,4.14) rot=(0,0,1;1.5708rad)
  shape: bbox 5.075 x 7.615 x 10 mm, 168 faces, 6 solids (baked)
FEATURE [Part::Feature] Part__Feature065  label="SOT89"
  Placement = pos=(38.4751,17.3184,0.94) rot=(0,0,1;1.5708rad)
  shape: bbox 7.1 x 6.5 x 1.6 mm, 80 faces (baked)
FEATURE [Part::Feature] Part__Feature066  label="1206 Tantalum"
  Placement = pos=(38.6251,22.3684,2.54) rot=(0,1,0;3.14159rad)
  shape: bbox 3.2 x 1.6 x 1.5 mm, 24 faces (baked)
FEATURE [Part::Feature] Part__Feature067  label="0603 Resistor004"
  Placement = pos=(38.4251,24.9684,2.54) rot=(0,1,0;3.14159rad)
  shape: bbox 1.6 x 0.8 x 0.5 mm, 69 faces (baked)
FEATURE [Part::Feature] Part__Feature068  label="0603 Capacitor"
  Placement = pos=(35.0338,14.4684,2.54) rot=(0,1,0;3.14159rad)
  shape: bbox 1.6 x 0.8 x 0.7 mm, 69 faces (baked)
FEATURE [Part::Feature] Part__Feature069  label="1206 Tantalum001"
  Placement = pos=(7.64506,24.3684,2.54) rot=(1,0,0;3.14159rad)
  shape: bbox 3.2 x 1.6 x 1.5 mm, 24 faces (baked)
FEATURE [Part::Feature] Part__Feature070  label="0603 Capacitor001"
  Placement = pos=(6.90589,22.4745,2.54) rot=(0,1,0;3.14159rad)
  shape: bbox 1.6 x 0.8 x 0.7 mm, 69 faces (baked)
FEATURE [Part::Feature] Part__Feature071  label="0603 Capacitor002"
  Placement = pos=(17.8451,14.0245,2.54) rot=(0,1,0;3.14159rad)
  shape: bbox 1.6 x 0.8 x 0.7 mm, 69 faces (baked)
FEATURE [Part::Feature] Part__Feature072  label="0603 Capacitor003"
  Placement = pos=(17.8451,15.0767,2.54) rot=(0,1,0;3.14159rad)
  shape: bbox 1.6 x 0.8 x 0.7 mm, 69 faces (baked)
FEATURE [Part::Feature] Part__Feature073  label="0603 Capacitor004"
  Placement = pos=(25.3451,21.2855,2.54) rot=(0,1,0;3.14159rad)
  shape: bbox 1.6 x 0.8 x 0.7 mm, 69 faces (baked)
FEATURE [Part::Feature] Part__Feature074  label="0603 Resistor005"
  Placement = pos=(23.8451,15.8601,2.54) rot=(0,1,0;3.14159rad)
  shape: bbox 1.6 x 0.8 x 0.5 mm, 69 faces (baked)
FEATURE [Part::Feature] Part__Feature075  label="0603 Resistor006"
  Placement = pos=(23.8451,14.4709,2.54) rot=(0,1,0;3.14159rad)
  shape: bbox 1.6 x 0.8 x 0.5 mm, 69 faces (baked)
FEATURE [Part::Feature] Part__Feature076  label="CSTCE Crystal001"
  Placement = pos=(13.1731,14.7184,2.53) rot=(0,1,0;3.14159rad)
  shape: bbox 3.2 x 1.35 x 0.71 mm, 47 faces (baked)
FEATURE [Part::Feature] Part__Feature077  label="SOIC16"
  Placement = pos=(16.6451,19.5642,2.54) rot=(0,1,0;3.14159rad)
  shape: bbox 10.2 x 6 x 1.5 mm, 154 faces (baked)
FEATURE [App::Part] Arduino_Nano  label="Arduino Nano001"
  Group = -> [Part__Feature051,Part__Feature052,ATMEGA328P_AU_STEP,Part__Feature054,Part__Feature055,Part__Feature056,Part__Feature057,Part__Feature058,Part__Feature059,Part__Feature060,Part__Feature061,Part__Feature062,Part__Feature063,Part__Feature064,Part__Feature065,Part__Feature066,Part__Feature067,Part__Feature068,Part__Feature069,Part__Feature070,Part__Feature071,Part__Feature072,Part__Feature073,+4 more]
  Origin = -> Origin006
  Placement = pos=(-73.5,-34.5,12.5) rot=(1,0,0;3.14159rad)
FEATURE [Part::Feature] Part__Feature078  label="Varsayılan"
  shape: bbox 42.6 x 16.1 x 5.9 mm, 343 faces, 7 solids (baked)
FEATURE [App::Part] f818e014b189db61e14b8aa713db12f520221103_1_5sl1wb  label="Bluetooth Module"
  Group = -> [Part__Feature078]
  Origin = -> Origin007
  Placement = pos=(-8,-91.75,41) rot=(-0.57735,-0.57735,0.57735;4.18879rad)
FEATURE [Mesh::Feature] Brilliant_Snicket__1_  label="Caster Marble Holder"
  Placement = pos=(-45,-110,4.88e-14) rot=(-1,0,0;3.14159rad)
FEATURE [Part::Sphere] Sphere  label="Marble"
  Angle1 = -90
  Angle2 = 90
  Angle3 = 360
  AttacherType = Attacher::AttachEngine3D
  Placement = pos=(0,-109.5,-9) rot=(0,0,1;0rad)
  Radius = 7.5
FEATURE [Part::Feature] Part__Feature045  label="INTERRUPTOR BASCULANTE"
  Placement = pos=(-83.5,-33.5,27) rot=(0.57735,-0.57735,-0.57735;4.18879rad)
  shape: bbox 15.1 x 17.9 x 10.42 mm, 555 faces, 4 solids (baked)
FEATURE [Part::Feature] Part__Feature088  label="Left Motor Lid"
  Placement = pos=(-56.5,0,2.5) rot=(0,0,1;0rad)
  shape: bbox 20 x 18 x 5.1 mm, 18 faces (baked)
FEATURE [Part::Feature] Part__Feature089  label="Right Motor Lid"
  Placement = pos=(36,0,2.5) rot=(0,0,1;0rad)
  shape: bbox 20 x 18 x 5.1 mm, 18 faces (baked)
FEATURE [Sketcher::SketchObject] Sketch037
  FullyConstrained = false
  sketch-geometry (43):
    g0: Circle CenterX=-84.0119 CenterY=-98.415 CenterZ=0 NormalX=0 NormalY=0 NormalZ=1 AngleXU=0 Radius=1
    g1: Circle CenterX=-71.6395 CenterY=-105.289 CenterZ=0 NormalX=0 NormalY=0 NormalZ=1 AngleXU=0 Radius=1
    g2: Circle CenterX=-64.6743 CenterY=-108.588 CenterZ=0 NormalX=0 NormalY=0 NormalZ=1 AngleXU=0 Radius=1
    g3: Circle CenterX=-54.9597 CenterY=-112.437 CenterZ=0 NormalX=0 NormalY=0 NormalZ=1 AngleXU=0 Radius=1
    g4: Circle CenterX=-46.7114 CenterY=-115.37 CenterZ=0 NormalX=0 NormalY=0 NormalZ=1 AngleXU=0 Radius=1
    g5: Circle CenterX=-37.8216 CenterY=-117.753 CenterZ=0 NormalX=0 NormalY=0 NormalZ=1 AngleXU=0 Radius=1
    g6: Circle CenterX=-29.4817 CenterY=-119.494 CenterZ=0 NormalX=0 NormalY=0 NormalZ=1 AngleXU=0 Radius=1
    g7: Circle CenterX=-15.3322 CenterY=-121.624 CenterZ=0 NormalX=0 NormalY=0 NormalZ=1 AngleXU=0 Radius=1
    g8: Circle CenterX=-5.70918 CenterY=-122.357 CenterZ=0 NormalX=0 NormalY=0 NormalZ=1 AngleXU=0 Radius=1
    g9: Circle CenterX=4.28038 CenterY=-122.357 CenterZ=0 NormalX=0 NormalY=0 NormalZ=1 AngleXU=0 Radius=1
    g10: Circle CenterX=14.9115 CenterY=-121.532 CenterZ=0 NormalX=0 NormalY=0 NormalZ=1 AngleXU=0 Radius=1
    g11: Circle CenterX=23.0681 CenterY=-120.524 CenterZ=0 NormalX=0 NormalY=0 NormalZ=1 AngleXU=0 Radius=1
    g12: Circle CenterX=32.5078 CenterY=-119.149 CenterZ=0 NormalX=0 NormalY=0 NormalZ=1 AngleXU=0 Radius=1
    g13: Circle CenterX=41.8558 CenterY=-116.689 CenterZ=0 NormalX=0 NormalY=0 NormalZ=1 AngleXU=0 Radius=1
    g14: Circle CenterX=49.5542 CenterY=-114.383 CenterZ=0 NormalX=0 NormalY=0 NormalZ=1 AngleXU=0 Radius=1
    g15: Circle CenterX=57.1609 CenterY=-111.817 CenterZ=0 NormalX=0 NormalY=0 NormalZ=1 AngleXU=0 Radius=1
    g16: Circle CenterX=63.2096 CenterY=-109.159 CenterZ=0 NormalX=0 NormalY=0 NormalZ=1 AngleXU=0 Radius=1
    g17: Circle CenterX=69.3538 CenterY=-106.481 CenterZ=0 NormalX=0 NormalY=0 NormalZ=1 AngleXU=0 Radius=1
    g18: Circle CenterX=75.1276 CenterY=-103.731 CenterZ=0 NormalX=0 NormalY=0 NormalZ=1 AngleXU=0 Radius=1
    g19: Circle CenterX=80.5348 CenterY=-100.615 CenterZ=0 NormalX=0 NormalY=0 NormalZ=1 AngleXU=0 Radius=1
    g20: Circle CenterX=84.2923 CenterY=-98.5073 CenterZ=0 NormalX=0 NormalY=0 NormalZ=1 AngleXU=0 Radius=1
    g21: LineSegment StartX=-84.0119 StartY=-98.415 StartZ=0 EndX=-71.6395 EndY=-105.289 EndZ=0
    g22: LineSegment StartX=-64.6743 StartY=-108.588 StartZ=0 EndX=-54.9597 EndY=-112.437 EndZ=0
    g23: LineSegment StartX=-46.7114 StartY=-115.37 StartZ=0 EndX=-37.8216 EndY=-117.753 EndZ=0
    g24: LineSegment StartX=-29.4817 StartY=-119.494 StartZ=0 EndX=-15.3322 EndY=-121.624 EndZ=0
    g25: LineSegment StartX=-5.70918 StartY=-122.357 StartZ=0 EndX=4.28038 EndY=-122.357 EndZ=0
    g26: LineSegment StartX=14.9115 StartY=-121.532 StartZ=0 EndX=23.0681 EndY=-120.524 EndZ=0
    g27: LineSegment StartX=32.5078 StartY=-119.149 StartZ=0 EndX=41.8558 EndY=-116.689 EndZ=0
    g28: LineSegment StartX=49.5542 StartY=-114.383 StartZ=0 EndX=57.1609 EndY=-111.817 EndZ=0
    g29: LineSegment StartX=63.2096 StartY=-109.159 StartZ=0 EndX=69.3538 EndY=-106.481 EndZ=0
    g30: LineSegment StartX=75.1276 StartY=-103.731 StartZ=0 EndX=80.5348 EndY=-100.615 EndZ=0
    g31: LineSegment StartX=-71.6395 StartY=-105.289 StartZ=0 EndX=-64.6743 EndY=-108.588 EndZ=0
    g32: LineSegment StartX=-54.9597 StartY=-112.437 StartZ=0 EndX=-46.7114 EndY=-115.37 EndZ=0
    g33: LineSegment StartX=-37.8216 StartY=-117.753 StartZ=0 EndX=-29.4817 EndY=-119.494 EndZ=0
    g34: LineSegment StartX=-15.2581 StartY=-121.831 StartZ=0 EndX=-15.3322 EndY=-121.624 EndZ=0
    g35: LineSegment StartX=-5.70918 StartY=-122.357 StartZ=0 EndX=-15.3322 EndY=-121.624 EndZ=0
    g36: LineSegment StartX=4.28038 StartY=-122.357 StartZ=0 EndX=14.9115 EndY=-121.532 EndZ=0
    g37: LineSegment StartX=23.0681 StartY=-120.524 StartZ=0 EndX=32.5078 EndY=-119.149 EndZ=0
    g38: LineSegment StartX=42.0827 StartY=-116.689 StartZ=0 EndX=41.8558 EndY=-116.689 EndZ=0
    g39: LineSegment StartX=49.5542 StartY=-114.383 StartZ=0 EndX=42.0827 EndY=-116.689 EndZ=0
    g40: LineSegment StartX=57.1609 StartY=-111.817 StartZ=0 EndX=63.2096 EndY=-109.159 EndZ=0
    g41: LineSegment StartX=69.3538 StartY=-106.481 StartZ=0 EndX=75.1276 EndY=-103.731 EndZ=0
    g42: LineSegment StartX=80.5348 StartY=-100.615 StartZ=0 EndX=84.2923 EndY=-98.5073 EndZ=0
  constraints (46):
    c: Weight(g0) = 1
    c: Equal(g0, g1-g20) x20
    c: Coincident(g21,g0)
    c: Coincident(g21,g1)
    c: Coincident(g22,g2)
    c: Coincident(g22,g3)
    c: Coincident(g23,g4)
    c: Coincident(g23,g5)
    c: Coincident(g24,g6)
    c: Coincident(g24,g7)
    c: Coincident(g25,g8)
    c: Coincident(g25,g9)
    c: Horizontal(g25)
    c: Coincident(g26,g10)
    c: Coincident(g26,g11)
    c: Coincident(g27,g12)
    c: Coincident(g27,g13)
    c: Coincident(g28,g14)
    c: Coincident(g28,g15)
    c: Coincident(g29,g16)
    c: Coincident(g29,g17)
    c: Coincident(g30,g18)
    c: Coincident(g30,g19)
    c: Coincident(g31,g21)
    c: Coincident(g31,g22)
    c: Coincident(g32,g22)
    c: Coincident(g32,g23)
    c: Coincident(g33,g23)
    c: Coincident(g33,g24)
    c: Coincident(g34,g24)
    c: Coincident(g35,g25)
    c: Coincident(g35,g24)
    c: Coincident(g36,g25)
    c: Coincident(g36,g26)
    c: Coincident(g37,g26)
    c: Coincident(g37,g27)
    c: Coincident(g38,g27)
    c: Horizontal(g38)
    c: Coincident(g39,g28)
    c: Coincident(g39,g38)
    c: Coincident(g40,g28)
    c: Coincident(g40,g29)
    c: Coincident(g41,g29)
    c: Coincident(g41,g30)
    c: Coincident(g42,g30)
    c: Coincident(g42,g20)
FEATURE [Part::Extrusion] Extrude
  Base = -> Sketch037
  Dir = (0,0,1)
  DirMode = 2
  FaceMakerClass = Part::FaceMakerBullseye
  LengthFwd = 28
  LengthRev = 0
  Placement = pos=(0,-32,0) rot=(0,0,1;0rad)
  Solid = false
  Symmetric = false
FEATURE [Part::Extrusion] Extrude036  label="Robot Front Hit Plank"
  Base = -> Extrude
  Dir = (0,1,0)
  DirMode = 0
  FaceMakerClass = Part::FaceMakerBullseye
  LengthFwd = 2
  LengthRev = 0
  Placement = pos=(0,30,4) rot=(0,0,1;0rad)
  Solid = false
  Symmetric = false
FEATURE [Part::Feature] Part__Feature129  label="Bluetooth Module Holder001"
  Placement = pos=(0,1.5,0) rot=(0,0,1;0rad)
  shape: bbox 20 x 4 x 33 mm, 10 faces (baked)
FEATURE [Part::MultiFuse] Fusion
  Refine = true
  Shapes = -> [Cut015,Part__Feature129]
FEATURE [Part::MultiFuse] Fusion019  label="Full Robot Body002"
  Refine = true
  Shapes = -> [Cut016,Fusion]
FEATURE [Sketcher::SketchObject] Sketch038
  FullyConstrained = false
  MapMode = 5
  Placement = pos=(5.67e-13,3.818e-13,35) rot=(0,0,1;0rad)
  Support = -> [Fusion019]
  sketch-geometry (8):
    g0: LineSegment StartX=8 StartY=-91 StartZ=0 EndX=8.5 EndY=-91 EndZ=0
    g1: LineSegment StartX=8.5 StartY=-91 StartZ=0 EndX=8.5 EndY=-93.2 EndZ=0
    g2: LineSegment StartX=8.5 StartY=-93.2 StartZ=0 EndX=8 EndY=-93.2 EndZ=0
    g3: LineSegment StartX=8 StartY=-93.2 StartZ=0 EndX=8 EndY=-91 EndZ=0
    g4: LineSegment StartX=-8 StartY=-91 StartZ=0 EndX=-8.5 EndY=-91 EndZ=0
    g5: LineSegment StartX=-8.5 StartY=-91 StartZ=0 EndX=-8.5 EndY=-93.2 EndZ=0
    g6: LineSegment StartX=-8.5 StartY=-93.2 StartZ=0 EndX=-8 EndY=-93.2 EndZ=0
    g7: LineSegment StartX=-8 StartY=-93.2 StartZ=0 EndX=-8 EndY=-91 EndZ=0
  constraints (20):
    c: Coincident(g0,g1)
    c: Coincident(g1,g2)
    c: Coincident(g2,g3)
    c: Coincident(g3,g0)
    c: Horizontal(g0)
    c: Horizontal(g2)
    c: Vertical(g1)
    c: Vertical(g3)
    c: DistanceY(g1,g1) = 2.2
    c: DistanceX(g0,g0) = 0.5
    c: DistanceX(g-2,g0) = 8
    c: DistanceY(g-1,g0) = -91
    c: Coincident(g4,g5)
    c: Coincident(g5,g6)
    c: Coincident(g6,g7)
    c: Coincident(g7,g4)
    c: Horizontal(g4)
    c: Horizontal(g6)
    c: Vertical(g5)
    c: Vertical(g7)
FEATURE [Part::Extrusion] Extrude037
  Base = -> Sketch038
  Dir = (1.62e-14,1.09e-14,1)
  DirMode = 2
  FaceMakerClass = Part::FaceMakerBullseye
  LengthFwd = -32
  LengthRev = 0
  Solid = true
  Symmetric = false
FEATURE [Part::Cut] Cut017
  Base = -> Fusion019
  Refine = true
  Tool = -> Extrude037
FEATURE [Sketcher::SketchObject] Sketch039
  FullyConstrained = false
  MapMode = 5
  Placement = pos=(0,0,0) rot=(1,0,0;3.14159rad)
  Support = -> [Cut017]
  sketch-geometry (2):
    g0: Circle CenterX=15.0302 CenterY=109.419 CenterZ=0 NormalX=0 NormalY=0 NormalZ=1 AngleXU=0 Radius=1.75
    g1: Circle CenterX=-15.0302 CenterY=109.419 CenterZ=0 NormalX=0 NormalY=0 NormalZ=1 AngleXU=0 Radius=1.75
  constraints (2):
    c: Diameter(g0) = 3.5
    c: Diameter(g1) = 3.5
FEATURE [Part::Extrusion] Extrude038
  Base = -> Sketch039
  Dir = (0,0,-1)
  DirMode = 2
  FaceMakerClass = Part::FaceMakerBullseye
  LengthFwd = 10
  LengthRev = 0
  Solid = true
  Symmetric = true
FEATURE [Part::Cut] Cut018
  Base = -> Cut017
  Refine = true
  Tool = -> Extrude038
FEATURE [Sketcher::SketchObject] Sketch040
  FullyConstrained = false
  MapMode = 5
  Placement = pos=(0,0,35) rot=(0,0,1;0rad)
  Support = -> [Cut018]
  sketch-geometry (16):
    g0: LineSegment StartX=-60 StartY=35.0902 StartZ=0 EndX=60 EndY=35.0902 EndZ=0
    g1: LineSegment StartX=60 StartY=35.0902 StartZ=0 EndX=60 EndY=-34.9098 EndZ=0
    g2: LineSegment StartX=60 StartY=-34.9098 StartZ=0 EndX=95 EndY=-34.9098 EndZ=0
    g3: LineSegment StartX=95 StartY=-34.9098 StartZ=0 EndX=95 EndY=-89.9098 EndZ=0
    g4: LineSegment StartX=-60 StartY=35.0902 StartZ=0 EndX=-60 EndY=-34.9098 EndZ=0
    g5: LineSegment StartX=-60 StartY=-34.9098 StartZ=0 EndX=-95 EndY=-34.9098 EndZ=0
    g6: LineSegment StartX=-95 StartY=-34.9098 StartZ=0 EndX=-95 EndY=-89.9098 EndZ=0
    g7: ArcOfCircle CenterX=0 CenterY=35.7609 CenterZ=0 NormalX=0 NormalY=0 NormalZ=1 AngleXU=0 Radius=157.538 StartAngle=4.06509 EndAngle=5.35968
    g8: LineSegment StartX=-9.19712 StartY=-90.0815 StartZ=0 EndX=10.8029 EndY=-90.0815 EndZ=0
    g9: LineSegment StartX=10.8029 StartY=-90.0815 StartZ=0 EndX=10.8029 EndY=-94.0815 EndZ=0
    g10: LineSegment StartX=10.8029 StartY=-94.0815 StartZ=0 EndX=-9.19712 EndY=-94.0815 EndZ=0
    g11: LineSegment StartX=-9.19712 StartY=-94.0815 StartZ=0 EndX=-9.19712 EndY=-90.0815 EndZ=0
    g12: Circle CenterX=70.8984 CenterY=-39.7159 CenterZ=0 NormalX=0 NormalY=0 NormalZ=1 AngleXU=0 Radius=1.5
    g13: Circle CenterX=37.3895 CenterY=29.2909 CenterZ=0 NormalX=0 NormalY=0 NormalZ=1 AngleXU=0 Radius=1.5
    g14: Circle CenterX=-37.6063 CenterY=29.3041 CenterZ=0 NormalX=0 NormalY=0 NormalZ=1 AngleXU=0 Radius=1.5
    g15: Circle CenterX=-67.6186 CenterY=-39.6843 CenterZ=0 NormalX=0 NormalY=0 NormalZ=1 AngleXU=0 Radius=1.5
  constraints (37):
    c: Horizontal(g0)
    c: Coincident(g0,g1)
    c: Vertical(g1)
    c: Coincident(g1,g2)
    c: Horizontal(g2)
    c: Coincident(g2,g3)
    c: Vertical(g3)
    c: Coincident(g0,g4)
    c: Vertical(g4)
    c: Coincident(g4,g5)
    c: Horizontal(g5)
    c: Coincident(g5,g6)
    c: Vertical(g6)
    c: DistanceX(g0,g0) = 120
    c: DistanceY(g1,g1) = 70
    c: Equal(g1,g4)
    c: DistanceX(g2,g2) = 35
    c: Equal(g2,g5)
    c: PointOnObject(g7,g-2)
    c: Coincident(g7,g6)
    c: Coincident(g7,g3)
    c: Equal(g3,g6)
    c: DistanceY(g3,g3) = 55
    c: Coincident(g8,g9)
    c: Coincident(g9,g10)
    c: Coincident(g10,g11)
    c: Coincident(g11,g8)
    c: Horizontal(g8)
    c: Horizontal(g10)
    c: Vertical(g9)
    c: Vertical(g11)
    c: DistanceX(g8,g8) = 20
    c: DistanceY(g9,g9) = 4
    c: Diameter(g12) = 3
    c: Diameter(g13) = 3
    c: Diameter(g14) = 3
    c: Diameter(g15) = 3
FEATURE [Part::Extrusion] Extrude039  label="Robot Lid"
  Base = -> Sketch040
  Dir = (0,0,1)
  DirMode = 2
  FaceMakerClass = Part::FaceMakerBullseye
  LengthFwd = 2
  LengthRev = 0
  Solid = true
  Symmetric = false
FEATURE [Part::Feature] Part__Feature131  label="MG90servo_shaft"
  Placement = pos=(16.5,28.5,-6.25) rot=(0,-1,0;0.664889rad)
  shape: bbox 5 x 4.3 x 5 mm, 110 faces (baked)
FEATURE [Part::Feature] Part__Feature133  label="BAttery"
  Placement = pos=(0,-59.5,2) rot=(0,0,1;0rad)
  shape: bbox 23 x 53 x 10 mm, 8 faces (baked)
FEATURE [Sketcher::SketchObject] Sketch041
  FullyConstrained = false
  MapMode = 5
  Placement = pos=(5.67e-13,3.818e-13,35) rot=(0,0,1;0rad)
  Support = -> [Cut018]
  sketch-geometry (8):
    g0: LineSegment StartX=9.30818 StartY=-44.7647 StartZ=0 EndX=11.5082 EndY=-44.7647 EndZ=0
    g1: LineSegment StartX=11.5082 StartY=-44.7647 StartZ=0 EndX=11.5082 EndY=-57.7647 EndZ=0
    g2: LineSegment StartX=11.5082 StartY=-57.7647 StartZ=0 EndX=9.30818 EndY=-57.7647 EndZ=0
    g3: LineSegment StartX=9.30818 StartY=-57.7647 StartZ=0 EndX=9.30818 EndY=-44.7647 EndZ=0
    g4: LineSegment StartX=-9.30818 StartY=-44.7647 StartZ=0 EndX=-11.5082 EndY=-44.7647 EndZ=0
    g5: LineSegment StartX=-11.5082 StartY=-44.7647 StartZ=0 EndX=-11.5082 EndY=-57.7647 EndZ=0
    g6: LineSegment StartX=-11.5082 StartY=-57.7647 StartZ=0 EndX=-9.30818 EndY=-57.7647 EndZ=0
    g7: LineSegment StartX=-9.30818 StartY=-57.7647 StartZ=0 EndX=-9.30818 EndY=-44.7647 EndZ=0
  constraints (18):
    c: Coincident(g0,g1)
    c: Coincident(g1,g2)
    c: Coincident(g2,g3)
    c: Coincident(g3,g0)
    c: Horizontal(g0)
    c: Horizontal(g2)
    c: Vertical(g1)
    c: Vertical(g3)
    c: DistanceX(g2,g2) = 2.2
    c: DistanceY(g1,g1) = 13
    c: Coincident(g4,g5)
    c: Coincident(g5,g6)
    c: Coincident(g6,g7)
    c: Coincident(g7,g4)
    c: Horizontal(g4)
    c: Horizontal(g6)
    c: Vertical(g5)
    c: Vertical(g7)
FEATURE [Part::Extrusion] Extrude040  label="Weapon Servo Slotter"
  Base = -> Sketch041
  Dir = (1.62e-14,1.09e-14,1)
  DirMode = 2
  FaceMakerClass = Part::FaceMakerBullseye
  LengthFwd = -27
  LengthRev = 0
  Solid = true
  Symmetric = false
FEATURE [Part::Cut] Cut019
  Base = -> Cut018
  Refine = true
  Tool = -> Extrude040
FEATURE [Sketcher::SketchObject] Sketch042
  FullyConstrained = false
  MapMode = 5
  Placement = pos=(-14.5,0,0) rot=(0.57735,-0.57735,-0.57735;2.0944rad)
  Support = -> [Cut019]
  sketch-geometry (4):
    g0: LineSegment StartX=44.5722 StartY=16.4536 StartZ=0 EndX=57.5722 EndY=16.4536 EndZ=0
    g1: LineSegment StartX=57.5722 StartY=16.4536 StartZ=0 EndX=57.5722 EndY=12.4536 EndZ=0
    g2: LineSegment StartX=57.5722 StartY=12.4536 StartZ=0 EndX=44.5722 EndY=12.4536 EndZ=0
    g3: LineSegment StartX=44.5722 StartY=12.4536 StartZ=0 EndX=44.5722 EndY=16.4536 EndZ=0
  constraints (10):
    c: Coincident(g0,g1)
    c: Coincident(g1,g2)
    c: Coincident(g2,g3)
    c: Coincident(g3,g0)
    c: Horizontal(g0)
    c: Horizontal(g2)
    c: Vertical(g1)
    c: Vertical(g3)
    c: DistanceX(g0,g0) = 13
    c: DistanceY(g1,g1) = 4
FEATURE [Part::Extrusion] Extrude041  label="Servo Wire Gap"
  Base = -> Sketch042
  Dir = (-1,0,0)
  DirMode = 2
  FaceMakerClass = Part::FaceMakerBullseye
  LengthFwd = 10
  LengthRev = 0
  Solid = true
  Symmetric = true
FEATURE [Part::Cut] Cut020
  Base = -> Cut019
  Refine = true
  Tool = -> Extrude041
FEATURE [Sketcher::SketchObject] Sketch043
  FullyConstrained = false
  MapMode = 5
  Placement = pos=(5.67e-13,3.818e-13,35) rot=(0,0,1;0rad)
  Support = -> [Cut020]
  sketch-geometry (2):
    g0: Circle CenterX=-13.6003 CenterY=-51.262 CenterZ=0 NormalX=0 NormalY=0 NormalZ=1 AngleXU=0 Radius=1
    g1: Circle CenterX=13.6003 CenterY=-51.262 CenterZ=0 NormalX=0 NormalY=0 NormalZ=1 AngleXU=0 Radius=1
  constraints (2):
    c: Diameter(g0) = 2
    c: Diameter(g1) = 2
FEATURE [Part::Extrusion] Extrude042  label="Servo Screw Guide"
  Base = -> Sketch043
  Dir = (1.62e-14,1.09e-14,1)
  DirMode = 2
  FaceMakerClass = Part::FaceMakerBullseye
  LengthFwd = -15
  LengthRev = 0
  Solid = true
  Symmetric = false
FEATURE [Part::Cut] Cut021  label="Robot Full Body"
  Base = -> Cut020
  Refine = true
  Tool = -> Extrude042
FEATURE [Sketcher::SketchObject] Sketch044
  FullyConstrained = false
  MapMode = 5
  Placement = pos=(0,0,38) rot=(0,0,1;0rad)
  Support = -> [Cut013]
  sketch-geometry (4):
    g0: LineSegment StartX=-17.5 StartY=-44.4409 StartZ=0 EndX=17.5 EndY=-44.4409 EndZ=0
    g1: LineSegment StartX=17.5 StartY=-44.4409 StartZ=0 EndX=17.5 EndY=-58.4409 EndZ=0
    g2: LineSegment StartX=17.5 StartY=-58.4409 StartZ=0 EndX=-17.5 EndY=-58.4409 EndZ=0
    g3: LineSegment StartX=-17.5 StartY=-58.4409 StartZ=0 EndX=-17.5 EndY=-44.4409 EndZ=0
  constraints (11):
    c: Coincident(g0,g1)
    c: Coincident(g1,g2)
    c: Coincident(g2,g3)
    c: Coincident(g3,g0)
    c: Horizontal(g0)
    c: Horizontal(g2)
    c: Vertical(g1)
    c: Vertical(g3)
    c: DistanceX(g0,g0) = 35
    c: DistanceY(g1,g1) = 14
    c: DistanceX(g-1,g1) = 17.5
FEATURE [Part::Extrusion] Extrude043  label="Servo Lid Gap"
  Base = -> Sketch044
  Dir = (0,0,1)
  DirMode = 2
  FaceMakerClass = Part::FaceMakerBullseye
  LengthFwd = 30
  LengthRev = 0
  Solid = true
  Symmetric = true
FEATURE [Part::Cut] Cut022
  Base = -> Extrude039
  Refine = true
  Tool = -> Extrude043
FEATURE [Part::Feature] Part__Feature135  label="Weapon Gear"
  Placement = pos=(15.25,-97.1218,73.3225) rot=(-1,0,0;0.349066rad)
  shape: bbox 5 x 28.28 x 28.28 mm, 34 faces (baked)
FEATURE [Sketcher::SketchObject] Sketch
  FullyConstrained = false
  MapMode = 5
  Placement = pos=(5.67e-13,3.818e-13,35) rot=(0,0,1;0rad)
  Support = -> [Cut021]
  sketch-geometry (4):
    g0: LineSegment StartX=-16.778 StartY=-44.4921 StartZ=0 EndX=16.4262 EndY=-44.4921 EndZ=0
    g1: LineSegment StartX=16.4262 StartY=-44.4921 StartZ=0 EndX=16.4262 EndY=-57.8256 EndZ=0
    g2: LineSegment StartX=16.4262 StartY=-57.8256 StartZ=0 EndX=-16.778 EndY=-57.8256 EndZ=0
    g3: LineSegment StartX=-16.778 StartY=-57.8256 StartZ=0 EndX=-16.778 EndY=-44.4921 EndZ=0
  constraints (8):
    c: Coincident(g0,g1)
    c: Coincident(g1,g2)
    c: Coincident(g2,g3)
    c: Coincident(g3,g0)
    c: Horizontal(g0)
    c: Horizontal(g2)
    c: Vertical(g1)
    c: Vertical(g3)
FEATURE [Part::Extrusion] Extrude044  label="Battery Walls Servo Gap"
  Base = -> Sketch
  Dir = (1.62e-14,1.09e-14,1)
  DirMode = 2
  FaceMakerClass = Part::FaceMakerBullseye
  LengthFwd = -5
  LengthRev = 0
  Solid = true
  Symmetric = false
FEATURE [Part::Cut] Cut023  label="Body001"
  Base = -> Cut021
  Refine = true
  Tool = -> Extrude044
FEATURE [Sketcher::SketchObject] Sketch045
  FullyConstrained = false
  Placement = pos=(0,0,0) rot=(0.57735,0.57735,0.57735;2.0944rad)
  sketch-geometry (15):
    g0: LineSegment StartX=-51 StartY=0 StartZ=0 EndX=-51 EndY=107.728 EndZ=0
    g1: LineSegment StartX=-86 StartY=37.2 StartZ=0 EndX=-86 EndY=39.2 EndZ=0
    g2: LineSegment StartX=-86 StartY=39.2 StartZ=0 EndX=-79 EndY=39.2 EndZ=0
    g3: LineSegment StartX=-79 StartY=39.2 StartZ=0 EndX=-79 EndY=64.2 EndZ=0
    g4: ArcOfCircle CenterX=-51 CenterY=37.2 CenterZ=0 NormalX=0 NormalY=0 NormalZ=1 AngleXU=0 Radius=38.8973 StartAngle=1.5708 EndAngle=2.37437
    g5: GeomPoint X=-85.9987 Y=37.2202 Z=0
    g6: GeomPoint X=-50.9998 Y=37.2065 Z=0
    g7: LineSegment StartX=-86 StartY=37.2 StartZ=0 EndX=-51 EndY=37.2 EndZ=0
    g8: LineSegment StartX=-16 StartY=37.2 StartZ=0 EndX=-16 EndY=39.2 EndZ=0
    g9: LineSegment StartX=-16 StartY=39.2 StartZ=0 EndX=-23 EndY=39.2 EndZ=0
    g10: LineSegment StartX=-23 StartY=39.2 StartZ=0 EndX=-23 EndY=64.2 EndZ=0
    g11: ArcOfCircle CenterX=-51 CenterY=37.2 CenterZ=0 NormalX=0 NormalY=0 NormalZ=1 AngleXU=0 Radius=38.8973 StartAngle=0.767218 EndAngle=1.5708
    g12: GeomPoint X=-16.0013 Y=37.2202 Z=0
    g13: GeomPoint X=-51.0002 Y=37.2065 Z=0
    g14: LineSegment StartX=-16 StartY=37.2 StartZ=0 EndX=-51 EndY=37.2 EndZ=0
  constraints (28):
    c: PointOnObject(g0,g-1)
    c: Vertical(g0)
    c: DistanceX(g-2,g0) = -51
    c: Vertical(g1)
    c: Coincident(g1,g2)
    c: Horizontal(g2)
    c: DistanceX(g2,g2) = 7
    c: DistanceY(g1,g1) = 2
    c: Coincident(g3,g2)
    c: Vertical(g3)
    c: PointOnObject(g4,g0)
    c: Coincident(g4,g3)
    c: PointOnObject(g4,g0)
    c: DistanceY(g3,g3) = 25
    c: Distance(g4,g1) = 35
    c: Coincident(g1,g7)
    c: Coincident(g7,g4)
    c: Horizontal(g7)
    c: Vertical(g8)
    c: Coincident(g8,g9)
    c: Horizontal(g9)
    c: Coincident(g10,g9)
    c: Vertical(g10)
    c: Coincident(g11,g10)
    c: Distance(g11,g8) = 35
    c: Coincident(g8,g14)
    c: Coincident(g14,g11)
    c: Horizontal(g14)
FEATURE [Part::Extrusion] Extrude045  label="Block"
  Base = -> Sketch045
  Dir = (1,0,0)
  DirMode = 2
  FaceMakerClass = Part::FaceMakerBullseye
  LengthFwd = 60
  LengthRev = 0
  Placement = pos=(-35.5,0,0) rot=(0,0,1;0rad)
  Solid = true
  Symmetric = false
FEATURE [Sketcher::SketchObject] Sketch046
  FullyConstrained = true
  MapMode = 45
  Placement = pos=(-5.5,-69.4459,37.2541) rot=(-0.003989,0.003989,0.999984;1.57081rad)
  Support = -> [Extrude045]
  sketch-geometry (4):
    g0: LineSegment StartX=16 StartY=-28 StartZ=0 EndX=-34 EndY=-28 EndZ=0
    g1: LineSegment StartX=-34 StartY=-28 StartZ=0 EndX=-34 EndY=26 EndZ=0
    g2: LineSegment StartX=-34 StartY=26 StartZ=0 EndX=16 EndY=26 EndZ=0
    g3: LineSegment StartX=16 StartY=26 StartZ=0 EndX=16 EndY=-28 EndZ=0
  constraints (12):
    c: Coincident(g0,g1)
    c: Coincident(g1,g2)
    c: Coincident(g2,g3)
    c: Coincident(g3,g0)
    c: Horizontal(g0)
    c: Horizontal(g2)
    c: Vertical(g1)
    c: Vertical(g3)
    c: DistanceY(g3,g3) = 54
    c: DistanceX(g0,g0) = 50
    c: Distance(g-1,g2) = 26
    c: Distance(g-1,g3) = 16
FEATURE [Part::Extrusion] Extrude046  label="Semi Hollower"
  Base = -> Sketch046
  Dir = (1e-16,0.00797758,0.999968)
  DirMode = 2
  FaceMakerClass = Part::FaceMakerBullseye
  LengthFwd = 24
  LengthRev = 0
  Placement = pos=(-0.75,27.25,-1) rot=(0,0,1;0rad)
  Solid = true
  Symmetric = false
FEATURE [Part::Cut] Cut024
  Base = -> Extrude045
  Refine = true
  Tool = -> Extrude046
FEATURE [Sketcher::SketchObject] Sketch047
  FullyConstrained = true
  MapMode = 5
  Placement = pos=(20.25,-97.1218,73.3225) rot=(0.497543,0.710565,0.497543;1.90603rad)
  Support = -> [Part__Feature135]
  sketch-geometry (1):
    g0: Circle CenterX=46.07 CenterY=0 CenterZ=0 NormalX=0 NormalY=0 NormalZ=1 AngleXU=0 Radius=4
  constraints (3):
    c: PointOnObject(g0,g-1)
    c: Diameter(g0) = 8
    c: Distance(g-1,g0) = 46.07
FEATURE [Part::Extrusion] Extrude047  label="Gear Axis"
  Base = -> Sketch047
  Dir = (1,4e-16,-5e-16)
  DirMode = 2
  FaceMakerClass = Part::FaceMakerBullseye
  LengthFwd = 8
  LengthRev = 0
  Solid = true
  Symmetric = false
FEATURE [Sketcher::SketchObject] Sketch048
  FullyConstrained = false
  MapMode = 5
  Placement = pos=(24.5,0,0) rot=(0.57735,0.57735,0.57735;2.0944rad)
  Support = -> [Cut024]
  sketch-geometry (1):
    g0: Circle CenterX=-51.7929 CenterY=59.9263 CenterZ=0 NormalX=0 NormalY=0 NormalZ=1 AngleXU=0 Radius=4.5
  constraints (1):
    c: Diameter(g0) = 9
FEATURE [Part::Extrusion] Extrude048  label="Axis Hole Lid"
  Base = -> Sketch048
  Dir = (1,0,0)
  DirMode = 2
  FaceMakerClass = Part::FaceMakerBullseye
  LengthFwd = 200
  LengthRev = 0
  Solid = true
  Symmetric = true
FEATURE [Part::Cut] Cut025
  Base = -> Cut024
  Refine = true
  Tool = -> Extrude048
FEATURE [Sketcher::SketchObject] Sketch049
  FullyConstrained = false
  MapMode = 5
  Placement = pos=(0,0,39.2) rot=(0,0,1;0rad)
  Support = -> [Cut025]
  sketch-geometry (12):
    g0: Circle CenterX=-29.075 CenterY=-82.7143 CenterZ=0 NormalX=0 NormalY=0 NormalZ=1 AngleXU=0 Radius=2
    g1: Circle CenterX=13.7546 CenterY=-82.7143 CenterZ=0 NormalX=0 NormalY=0 NormalZ=1 AngleXU=0 Radius=2
    g2: LineSegment StartX=0 StartY=-86.2143 StartZ=0 EndX=-45.2023 EndY=-86.2143 EndZ=0
    g3: LineSegment StartX=0 StartY=-86.2143 StartZ=0 EndX=32.2889 EndY=-86.2143 EndZ=0
    g4: LineSegment StartX=0 StartY=-51.8014 StartZ=0 EndX=47.4966 EndY=-51.8014 EndZ=0
    g5: LineSegment StartX=0 StartY=-16.0163 StartZ=0 EndX=-56.9256 EndY=-16.0163 EndZ=0
    g6: LineSegment StartX=0 StartY=-16.0163 StartZ=0 EndX=36.7372 EndY=-16.0163 EndZ=0
    g7: LineSegment StartX=14.2686 StartY=-82.7143 StartZ=0 EndX=13.7546 EndY=-82.7143 EndZ=0
    g8: LineSegment StartX=13.7546 StartY=-82.7143 StartZ=0 EndX=13.7546 EndY=-4.0407 EndZ=0
    g9: LineSegment StartX=-29.075 StartY=-82.7143 StartZ=0 EndX=-29.075 EndY=0.808399 EndZ=0
    g10: Circle CenterX=-29.075 CenterY=-19.5163 CenterZ=0 NormalX=0 NormalY=0 NormalZ=1 AngleXU=0 Radius=2
    g11: Circle CenterX=13.7546 CenterY=-19.5163 CenterZ=0 NormalX=0 NormalY=0 NormalZ=1 AngleXU=0 Radius=2
  constraints (26):
    c: Diameter(g1) = 4
    c: Diameter(g0) = 4
    c: PointOnObject(g2,g-2)
    c: Horizontal(g2)
    c: Coincident(g3,g2)
    c: Horizontal(g3)
    c: Distance(g1,g3) = 3.5
    c: Distance(g0,g2) = 3.5
    c: PointOnObject(g4,g-2)
    c: Horizontal(g4)
    c: PointOnObject(g5,g-2)
    c: Horizontal(g5)
    c: Coincident(g6,g5)
    c: Horizontal(g6)
    c: Coincident(g7,g1)
    c: Horizontal(g7)
    c: Coincident(g8,g1)
    c: Vertical(g8)
    c: Coincident(g9,g0)
    c: Vertical(g9)
    c: PointOnObject(g10,g9)
    c: Diameter(g10) = 4
    c: Distance(g10,g5) = 3.5
    c: PointOnObject(g11,g8)
    c: Diameter(g11) = 4
    c: Distance(g11,g6) = 3.5
FEATURE [Part::Extrusion] Extrude049  label="Weapon Cover Screw Holes"
  Base = -> Sketch049
  Dir = (0,0,1)
  DirMode = 2
  FaceMakerClass = Part::FaceMakerBullseye
  LengthFwd = 30
  LengthRev = 0
  Solid = true
  Symmetric = true
FEATURE [Part::Extrusion] Extrude050  label="Weapon Cover Screw Holes001"
  Base = -> Sketch049
  Dir = (0,0,1)
  DirMode = 2
  FaceMakerClass = Part::FaceMakerBullseye
  LengthFwd = 30
  LengthRev = 0
  Solid = true
  Symmetric = true
FEATURE [Part::Cut] Cut026
  Base = -> Cut025
  Refine = true
  Tool = -> Extrude049
FEATURE [Sketcher::SketchObject] Sketch050
  FullyConstrained = false
  MapMode = 5
  Placement = pos=(-35.5,0,0) rot=(0.57735,-0.57735,-0.57735;2.0944rad)
  Support = -> [Cut026]
  sketch-geometry (7):
    g0: LineSegment StartX=24.0671 StartY=62.8288 StartZ=0 EndX=24.0671 EndY=39.5462 EndZ=0
    g1: LineSegment StartX=24.0671 StartY=39.5462 StartZ=0 EndX=78.0671 EndY=39.5462 EndZ=0
    g2: LineSegment StartX=24.0671 StartY=62.8288 StartZ=0 EndX=78.136 EndY=62.8288 EndZ=0
    g3: LineSegment StartX=23.0671 StartY=64.1604 StartZ=0 EndX=23.0671 EndY=39.2199 EndZ=0
    g4: LineSegment StartX=79.0671 StartY=64.1714 StartZ=0 EndX=79.0671 EndY=39.1859 EndZ=0
    g5: ArcOfCircle CenterX=51.0103 CenterY=36.4308 CenterZ=0 NormalX=0 NormalY=0 NormalZ=1 AngleXU=0 Radius=37.7199 StartAngle=0.770865 EndAngle=2.36641
    g6: LineSegment StartX=78.0671 StartY=62.7123 StartZ=0 EndX=78.0671 EndY=39.5462 EndZ=0
  constraints (13):
    c: Vertical(g0)
    c: Coincident(g0,g1)
    c: Horizontal(g1)
    c: Coincident(g0,g2)
    c: Horizontal(g2)
    c: Vertical(g3)
    c: Distance(g0,g3) = 1
    c: Vertical(g4)
    c: Coincident(g5,g0)
    c: Distance(g1,g4) = 1
    c: Coincident(g6,g5)
    c: Coincident(g6,g1)
    c: Vertical(g6)
FEATURE [Part::Extrusion] Extrude051  label="Block Hollower"
  Base = -> Sketch050
  Dir = (-1,0,0)
  DirMode = 2
  FaceMakerClass = Part::FaceMakerBullseye
  LengthFwd = 56
  LengthRev = 0
  Placement = pos=(57.5,0,0) rot=(0,0,1;0rad)
  Solid = true
  Symmetric = false
FEATURE [Part::MultiFuse] Fusion020
  Refine = true
  Shapes = -> [Part__Feature135,Extrude047]
FEATURE [Sketcher::SketchObject] Sketch051
  FullyConstrained = false
  MapMode = 5
  Placement = pos=(28.25,2.8e-15,-1.64e-14) rot=(0.57735,0.57735,0.57735;2.0944rad)
  Support = -> [Fusion020]
  sketch-geometry (1):
    g0: Circle CenterX=-53.8481 CenterY=57.5893 CenterZ=0 NormalX=0 NormalY=0 NormalZ=1 AngleXU=0 Radius=1.5
  constraints (1):
    c: Diameter(g0) = 3
FEATURE [Part::Extrusion] Extrude052  label="Weapon Screw"
  Base = -> Sketch051
  Dir = (1,-2e-16,-7e-16)
  DirMode = 2
  FaceMakerClass = Part::FaceMakerBullseye
  LengthFwd = -8
  LengthRev = 0
  Solid = true
  Symmetric = false
FEATURE [Part::Cut] Cut029  label="Weapon Gear001"
  Base = -> Fusion020
  Placement = pos=(0,2.25,2.25) rot=(0,0,1;0rad)
  Refine = true
  Tool = -> Extrude052
FEATURE [Sketcher::SketchObject] Sketch052
  FullyConstrained = false
  MapMode = 5
  Placement = pos=(15.25,2.25,2.25) rot=(0.57735,-0.57735,-0.57735;2.0944rad)
  Support = -> [Cut029]
  sketch-geometry (2):
    g0: Circle CenterX=53.7296 CenterY=57.4712 CenterZ=0 NormalX=0 NormalY=0 NormalZ=1 AngleXU=0 Radius=9.92397
    g1: Circle CenterX=53.7296 CenterY=57.4712 CenterZ=0 NormalX=0 NormalY=0 NormalZ=1 AngleXU=0 Radius=4
  constraints (2):
    c: Coincident(g1,g0)
    c: Diameter(g1) = 8
FEATURE [Sketcher::SketchObject] Sketch053
  FullyConstrained = false
  sketch-geometry (10):
    g0: LineSegment StartX=-48.1822 StartY=-117.243 StartZ=0 EndX=-37.0056 EndY=-120.416 EndZ=0
    g1: LineSegment StartX=-29.0026 StartY=-121.796 StartZ=0 EndX=-37.0056 EndY=-120.416 EndZ=0
    g2: LineSegment StartX=-29.0026 StartY=-121.796 StartZ=0 EndX=-16.4463 EndY=-123.728 EndZ=0
    g3: LineSegment StartX=-16.4463 StartY=-123.728 StartZ=0 EndX=-5.13172 EndY=-124.556 EndZ=0
    g4: LineSegment StartX=-5.13172 StartY=-124.556 StartZ=0 EndX=4.38905 EndY=-124.556 EndZ=0
    g5: LineSegment StartX=4.38905 StartY=-124.556 StartZ=0 EndX=13.7718 EndY=-123.866 EndZ=0
    g6: LineSegment StartX=13.7718 StartY=-123.866 StartZ=0 EndX=22.6027 EndY=-122.9 EndZ=0
    g7: LineSegment StartX=22.6027 StartY=-122.9 StartZ=0 EndX=30.4677 EndY=-121.658 EndZ=0
    g8: LineSegment StartX=30.4677 StartY=-121.658 StartZ=0 EndX=37.7807 EndY=-120.002 EndZ=0
    g9: LineSegment StartX=37.7807 StartY=-120.002 StartZ=0 EndX=46.7496 EndY=-117.657 EndZ=0
  constraints (4):
    c: Coincident(g1,g0)
    c: Coincident(g2,g1)
    c: Coincident(g3,g2)
    c: Horizontal(g4)
FEATURE [Part::Extrusion] Extrude054
  Base = -> Sketch053
  Dir = (0,0,1)
  DirMode = 2
  FaceMakerClass = Part::FaceMakerBullseye
  LengthFwd = 23
  LengthRev = 0
  Solid = false
  Symmetric = false
FEATURE [Part::Extrusion] Extrude057  label="Front Hit Plank 2"
  Base = -> Extrude054
  Dir = (0,1,0)
  DirMode = 0
  FaceMakerClass = Part::FaceMakerBullseye
  LengthFwd = -1
  LengthRev = 0
  Placement = pos=(0,0.25,6) rot=(0,0,1;0rad)
  Solid = false
  Symmetric = false
FEATURE [Part::Cut] Cut027  label="Lid"
  Base = -> Cut022
  Refine = true
  Tool = -> Extrude050
FEATURE [Part::Feature] Part__Feature132  label="MG90servo_gear"
  Placement = pos=(16.5,34.45,-6.25) rot=(0.999878,0,0.015592;3.14159rad)
  shape: bbox 34.99 x 4.85 x 16.29 mm, 61 faces (baked)
FEATURE [Part::Feature] Part__Feature130  label="MG90servo_body"
  shape: bbox 32.05 x 28.5 x 13.53 mm, 90 faces (baked)
FEATURE [App::Part] MG90servo_assembly
  Group = -> [Part__Feature130,Part__Feature131,Part__Feature132]
  Origin = -> Origin008
  Placement = pos=(11.25,-44.75,12) rot=(0,-0.707107,-0.707107;3.14159rad)
FEATURE [Part::Feature] Part__Feature134  label="Servo Gear Mount"
  Placement = pos=(-21.4289,-43.9017,80.99) rot=(-0.999315,0.026168,-0.026168;1.57148rad)
  shape: bbox 49.99 x 49.99 x 5 mm, 79 faces (baked)
FEATURE [Part::Extrusion] Extrude053  label="Weapon Left Axle"
  Base = -> Sketch052
  Dir = (-1,0,0)
  DirMode = 2
  FaceMakerClass = Part::FaceMakerBullseye
  LengthFwd = 53
  LengthRev = 0
  Solid = true
  Symmetric = false
FEATURE [Mesh::Feature] Powerful_Trug__4_  label="Axe"
  Placement = pos=(37.5,-21,56.75) rot=(0,1,0;4.71239rad)
FEATURE [Part::Cut] Cut028  label="Weapon Gear Cover"
  Base = -> Cut026
  Refine = true
  Tool = -> Extrude051
FEATURE [Sketcher::SketchObject] Sketch054
  FullyConstrained = false
  MapMode = 5
  Placement = pos=(66.5738,-109.804,4) rot=(0.952554,0.215221,0.215221;1.61939rad)
  Support = -> [Extrude036]
  sketch-geometry (1):
    g0: Circle CenterX=0 CenterY=19.7495 CenterZ=0 NormalX=0 NormalY=0 NormalZ=1 AngleXU=0 Radius=2
  constraints (2):
    c: PointOnObject(g0,g-2)
    c: Diameter(g0) = 4
FEATURE [Part::Extrusion] Extrude058
  Base = -> Sketch054
  Dir = (0.429935,-0.90286,-6e-16)
  DirMode = 2
  FaceMakerClass = Part::FaceMakerBullseye
  LengthFwd = 10
  LengthRev = 0
  Solid = true
  Symmetric = true
FEATURE [Part::Extrusion] Extrude059
  Base = -> Sketch054
  Dir = (0.429935,-0.90286,-6e-16)
  DirMode = 2
  FaceMakerClass = Part::FaceMakerBullseye
  LengthFwd = 10
  LengthRev = 0
  Placement = pos=(0,0,-13) rot=(0,0,1;0rad)
  Solid = true
  Symmetric = true
FEATURE [Sketcher::SketchObject] Sketch055
  FullyConstrained = false
  MapMode = 5
  Placement = pos=(32.0395,-122.254,6) rot=(0.98386,0.126531,0.126531;1.58707rad)
  Support = -> [Extrude057]
  sketch-geometry (2):
    g0: Circle CenterX=0 CenterY=17.6116 CenterZ=0 NormalX=0 NormalY=0 NormalZ=1 AngleXU=0 Radius=2
    g1: Circle CenterX=0 CenterY=5.94641 CenterZ=0 NormalX=0 NormalY=0 NormalZ=1 AngleXU=0 Radius=2
  constraints (4):
    c: PointOnObject(g0,g-2)
    c: Diameter(g0) = 4
    c: PointOnObject(g1,g-2)
    c: Diameter(g1) = 4
FEATURE [Part::Extrusion] Extrude060
  Base = -> Sketch055
  Dir = (0.253028,-0.967459,2e-16)
  DirMode = 2
  FaceMakerClass = Part::FaceMakerBullseye
  LengthFwd = 15
  LengthRev = 0
  Solid = true
  Symmetric = true
FEATURE [Sketcher::SketchObject] Sketch056
  FullyConstrained = false
  MapMode = 5
  Placement = pos=(-34.665,-121.831,6) rot=(0.981163,-0.136601,-0.136601;1.58981rad)
  Support = -> [Extrude057]
  sketch-geometry (2):
    g0: Circle CenterX=0 CenterY=18.3678 CenterZ=0 NormalX=0 NormalY=0 NormalZ=1 AngleXU=0 Radius=2
    g1: Circle CenterX=0 CenterY=6.57646 CenterZ=0 NormalX=0 NormalY=0 NormalZ=1 AngleXU=0 Radius=2
  constraints (4):
    c: PointOnObject(g0,g-2)
    c: PointOnObject(g1,g-2)
    c: Diameter(g1) = 4
    c: Diameter(g0) = 4
FEATURE [Part::Extrusion] Extrude061
  Base = -> Sketch056
  Dir = (-0.273152,-0.961971,0)
  DirMode = 2
  FaceMakerClass = Part::FaceMakerBullseye
  LengthFwd = 15
  LengthRev = 0
  Solid = true
  Symmetric = true
FEATURE [Sketcher::SketchObject] Sketch057
  FullyConstrained = false
  MapMode = 5
  Placement = pos=(-75.179,-105.322,4) rot=(0.938939,-0.243304,-0.243304;1.63376rad)
  Support = -> [Extrude036]
  sketch-geometry (2):
    g0: Circle CenterX=0 CenterY=20.5924 CenterZ=0 NormalX=0 NormalY=0 NormalZ=1 AngleXU=0 Radius=2
    g1: Circle CenterX=0 CenterY=8.18698 CenterZ=0 NormalX=0 NormalY=0 NormalZ=1 AngleXU=0 Radius=2
  constraints (4):
    c: PointOnObject(g0,g-2)
    c: PointOnObject(g1,g-2)
    c: Diameter(g1) = 4
    c: Diameter(g0) = 4
FEATURE [Part::Extrusion] Extrude062
  Base = -> Sketch057
  Dir = (-0.485643,-0.874157,-3e-16)
  DirMode = 2
  FaceMakerClass = Part::FaceMakerBullseye
  LengthFwd = 15
  LengthRev = 0
  Solid = true
  Symmetric = true
FEATURE [Part::MultiFuse] Fusion021  label="Front 2 Covers Holes"
  Refine = true
  Shapes = -> [Extrude060,Extrude061]
FEATURE [Part::MultiFuse] Fusion022  label="Side Covers Holes"
  Refine = true
  Shapes = -> [Extrude062,Extrude059,Extrude058]
FEATURE [Part::MultiFuse] Fusion023  label="Front 2 Covers Holes001"
  Refine = true
  Shapes = -> [Extrude060,Extrude061]
FEATURE [Part::MultiFuse] Fusion024  label="Front 2 Covers Holes002"
  Refine = true
  Shapes = -> [Extrude060,Extrude061]
FEATURE [Part::Cut] Cut030  label="Front Hit Pannel Layer 1"
  Base = -> Extrude057
  Refine = true
  Tool = -> Fusion021
FEATURE [Part::Cut] Cut031
  Base = -> Extrude036
  Refine = true
  Tool = -> Fusion023
FEATURE [Part::Cut] Cut032
  Base = -> Cut023
  Refine = true
  Tool = -> Fusion024
FEATURE [Part::MultiFuse] Fusion025  label="Side Covers Holes001"
  Refine = true
  Shapes = -> [Extrude062,Extrude059,Extrude058]
FEATURE [Part::Cut] Cut033  label="Front Hit Pannel Layer 2"
  Base = -> Cut031
  Refine = true
  Tool = -> Fusion025
FEATURE [Part::Cut] Cut034  label="Full Holed Body"
  Base = -> Cut032
  Refine = true
  Tool = -> Fusion022
FEATURE [Part::Feature] Part__Feature136  label="PCB MX1508"
  shape: bbox 24.5 x 1.62 x 21.2 mm, 502 faces (baked)
FEATURE [Part::Feature] Part__Feature137  label="smd100uF16VRVT"
  Placement = pos=(3.4012,1.65,-5.66553) rot=(0,-1,0;1.57952rad)
  shape: bbox 8.064 x 5.76 x 9.017 mm, 161 faces, 6 solids (baked)
FEATURE [Part::Feature] Part__Feature138  label="smd100uF16VRVT001"
  Placement = pos=(-3.69416,1.65,-5.66553) rot=(0,1,0;1.55334rad)
  shape: bbox 8.063 x 5.76 x 9.034 mm, 161 faces, 6 solids (baked)
FEATURE [Part::Feature] Part__Feature139  label="smdChip16pin"
  Placement = pos=(0.38974,1.52498,9.68189) rot=(0,1,0;3.14159rad)
  shape: bbox 7.3 x 1.227 x 10 mm, 477 faces, 17 solids (baked)
FEATURE [Part::Feature] Part__Feature140  label="smdResistor2200"
  Placement = pos=(10.7501,0.8,-6.22873) rot=(0,1,0;1.5708rad)
  shape: bbox 1.307 x 0.6262 x 2.511 mm, 79 faces, 3 solids (baked)
FEATURE [Part::Feature] Part__Feature141  label="smdDiode"
  Placement = pos=(8.50324,1.45,-6.59956) rot=(0,1,0;1.5708rad)
  shape: bbox 1.407 x 1.407 x 3.85 mm, 60 faces (baked)
FEATURE [App::Part] MX1508
  Group = -> [Part__Feature136,Part__Feature137,Part__Feature138,Part__Feature139,Part__Feature140,Part__Feature141]
  Origin = -> Origin009
  Placement = pos=(0,7.25,3) rot=(1,0,0;1.5708rad)
note: 1 file-system path scrubbed to <path> (originals preserved in the JSON sidecar)
